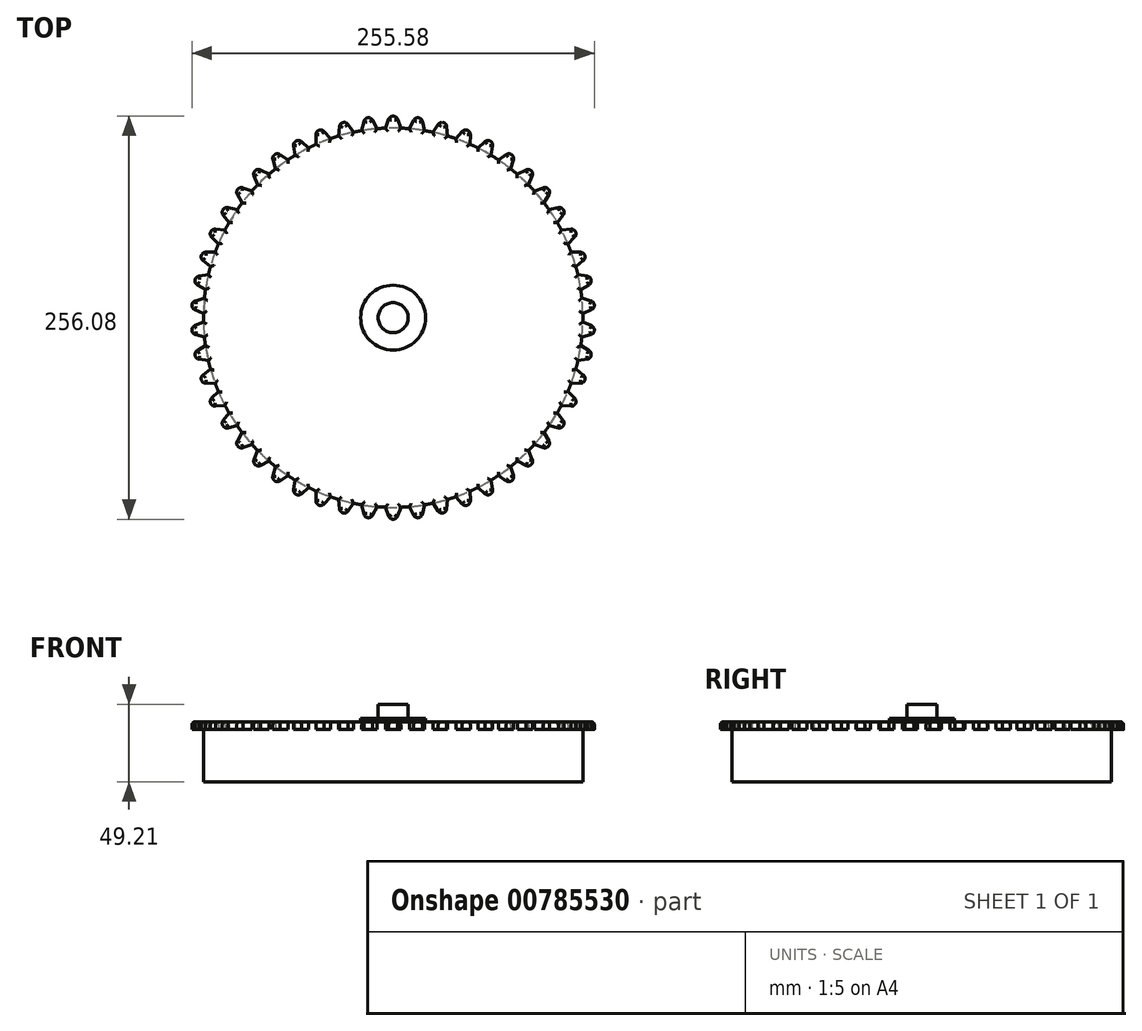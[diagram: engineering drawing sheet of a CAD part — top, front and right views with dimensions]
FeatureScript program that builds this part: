
annotation { "Feature Type Name" : "Feature", "Feature Type Description" : "" }
export const myFeature = defineFeature(function(context is Context, id is Id, definition is map)
    precondition{}
    {
        {
            var Q0;
            Q0=qCreatedBy(makeId("Top.planeOp"),FACE);
            var sketch = newSketch(context, id + "F0", { "sketchPlane" : qUnion([Q0])});
            skCircle(sketch, "E0", {"center": v(0, 0) * mm, "radius": 120.5 * mm});
            skSolve(sketch);
        }
        {
            var Q0;
            Q0 = qSketchRegion(id + "F0", true);
            extrude(context, id + "F1", {"entities" : qUnion([Q0]), "depth" : 38.1 * mm, "offsetDistance" : 25 * mm});
        }
        {
            var Q0;
            Q0=makeQuery(id+"F1.opExtrude","CAP_FACE",FACE,{"disambiguationData":[OSD([sQuery(id+"F0.wireOp",EDGE,"E0")])],"isStart":false});
            var sketch = newSketch(context, id + "F2", { "sketchPlane" : qUnion([Q0])});
            skCircle(sketch, "E1", {"center": v(0, 0) * mm, "radius": 9.53 * mm});
            skSolve(sketch);
        }
        {
            var Q0;
            Q0 = qSketchRegion(id + "F2", true);
            extrude(context, id + "F3", {"entities" : qUnion([Q0]), "operationType" : NewBodyOperationType.ADD, "depth" : 11.1 * mm, "offsetDistance" : 25 * mm});
        }
        {
            var Q0;
            Q0=makeQuery(id+"F1.opExtrude","CAP_FACE",FACE,{"disambiguationData":[OSD([sQuery(id+"F0.wireOp",EDGE,"E0")])],"isStart":false});
            var sketch = newSketch(context, id + "F4", { "sketchPlane" : qUnion([Q0])});
            skCircle(sketch, "E2", {"center": v(0, 0) * mm, "radius": 20.64 * mm});
            skSolve(sketch);
        }
        {
            var Q0;
            Q0 = qSketchRegion(id + "F4", true);
            extrude(context, id + "F5", {"entities" : qUnion([Q0]), "operationType" : NewBodyOperationType.ADD, "depth" : 2 * mm, "offsetDistance" : 25 * mm});
        }
        {
            var Q0;
            Q0=makeQuery(id+"F1.opExtrude","CAP_FACE",FACE,{"disambiguationData":[OSD([sQuery(id+"F0.wireOp",EDGE,"E0")])],"isStart":false});
            var sketch = newSketch(context, id + "F6", { "sketchPlane" : qUnion([Q0])});
            skLineSegment(sketch, "E3", {"start": v(-5, 120) * mm, "end": v(-2.8, 126.04) * mm});
            skLineSegment(sketch, "E4", {"start": v(-2.8, 126.04) * mm, "end": v(2.8, 126.04) * mm, "construction": true});
            skLineSegment(sketch, "E5", {"start": v(2.8, 126.04) * mm, "end": v(5, 120) * mm});
            skArc(sketch, "E6", {"start": v(2.8, 126.04) * mm, "mid": v(0, 128.04) * mm, "end": v(-2.8, 126.04) * mm});
            skPoint(sketch, "E7", {"position": v(0, 128.04) * mm});
            skLineSegment(sketch, "E8", {"start": v(5, 120) * mm, "end": v(7.52, 119.56) * mm});
            skLineSegment(sketch, "E9", {"start": v(-5, 120) * mm, "end": v(-7.52, 119.56) * mm});
            skArc(sketch, "E10.1.0", {"start": v(-13.02, 125.4) * mm, "mid": v(-16.05, 127.03) * mm, "end": v(-18.58, 124.7) * mm});
            skLineSegment(sketch, "E10.1.1", {"start": v(-10.08, 119.68) * mm, "end": v(-7.52, 119.56) * mm});
            skPoint(sketch, "E10.1.2", {"position": v(-16.05, 127.03) * mm});
            skLineSegment(sketch, "E10.1.3", {"start": v(-13.02, 125.4) * mm, "end": v(-10.08, 119.68) * mm});
            skLineSegment(sketch, "E10.1.4", {"start": v(-20, 118.43) * mm, "end": v(-22.45, 117.67) * mm});
            skLineSegment(sketch, "E10.1.5", {"start": v(-20, 118.43) * mm, "end": v(-18.58, 124.7) * mm});
            skLineSegment(sketch, "E10.1.6", {"start": v(-18.58, 124.7) * mm, "end": v(-13.02, 125.4) * mm, "construction": true});
            skArc(sketch, "E10.2.0", {"start": v(-28.63, 122.78) * mm, "mid": v(-31.84, 124.02) * mm, "end": v(-34.06, 121.38) * mm});
            skLineSegment(sketch, "E10.2.1", {"start": v(-25, 117.47) * mm, "end": v(-22.45, 117.67) * mm});
            skPoint(sketch, "E10.2.2", {"position": v(-31.84, 124.02) * mm});
            skLineSegment(sketch, "E10.2.3", {"start": v(-28.63, 122.78) * mm, "end": v(-25, 117.47) * mm});
            skLineSegment(sketch, "E10.2.4", {"start": v(-34.69, 114.99) * mm, "end": v(-37.02, 113.93) * mm});
            skLineSegment(sketch, "E10.2.5", {"start": v(-34.69, 114.99) * mm, "end": v(-34.06, 121.38) * mm});
            skLineSegment(sketch, "E10.2.6", {"start": v(-34.06, 121.38) * mm, "end": v(-28.63, 122.78) * mm, "construction": true});
            skArc(sketch, "E10.3.0", {"start": v(-43.8, 118.22) * mm, "mid": v(-47.13, 119.05) * mm, "end": v(-49, 116.16) * mm});
            skLineSegment(sketch, "E10.3.1", {"start": v(-39.53, 113.41) * mm, "end": v(-37.02, 113.93) * mm});
            skPoint(sketch, "E10.3.2", {"position": v(-47.13, 119.05) * mm});
            skLineSegment(sketch, "E10.3.3", {"start": v(-43.8, 118.22) * mm, "end": v(-39.53, 113.41) * mm});
            skLineSegment(sketch, "E10.3.4", {"start": v(-48.82, 109.73) * mm, "end": v(-51, 108.4) * mm});
            skLineSegment(sketch, "E10.3.5", {"start": v(-48.82, 109.73) * mm, "end": v(-49, 116.16) * mm});
            skLineSegment(sketch, "E10.3.6", {"start": v(-49, 116.16) * mm, "end": v(-43.8, 118.22) * mm, "construction": true});
            skArc(sketch, "E10.4.0", {"start": v(-58.26, 111.8) * mm, "mid": v(-61.68, 112.2) * mm, "end": v(-63.18, 109.1) * mm});
            skLineSegment(sketch, "E10.4.1", {"start": v(-53.43, 107.57) * mm, "end": v(-51, 108.4) * mm});
            skPoint(sketch, "E10.4.2", {"position": v(-61.68, 112.2) * mm});
            skLineSegment(sketch, "E10.4.3", {"start": v(-58.26, 111.8) * mm, "end": v(-53.43, 107.57) * mm});
            skLineSegment(sketch, "E10.4.4", {"start": v(-62.2, 102.75) * mm, "end": v(-64.19, 101.14) * mm});
            skLineSegment(sketch, "E10.4.5", {"start": v(-62.2, 102.75) * mm, "end": v(-63.18, 109.1) * mm});
            skLineSegment(sketch, "E10.4.6", {"start": v(-63.18, 109.1) * mm, "end": v(-58.26, 111.8) * mm, "construction": true});
            skArc(sketch, "E10.5.0", {"start": v(-71.82, 103.61) * mm, "mid": v(-75.26, 103.58) * mm, "end": v(-76.35, 100.32) * mm});
            skLineSegment(sketch, "E10.5.1", {"start": v(-66.49, 100.02) * mm, "end": v(-64.19, 101.14) * mm});
            skPoint(sketch, "E10.5.2", {"position": v(-75.26, 103.58) * mm});
            skLineSegment(sketch, "E10.5.3", {"start": v(-71.82, 103.61) * mm, "end": v(-66.49, 100.02) * mm});
            skLineSegment(sketch, "E10.5.4", {"start": v(-74.58, 94.14) * mm, "end": v(-76.36, 92.3) * mm});
            skLineSegment(sketch, "E10.5.5", {"start": v(-74.58, 94.14) * mm, "end": v(-76.35, 100.32) * mm});
            skLineSegment(sketch, "E10.5.6", {"start": v(-76.35, 100.32) * mm, "end": v(-71.82, 103.61) * mm, "construction": true});
            skArc(sketch, "E10.6.0", {"start": v(-84.24, 93.8) * mm, "mid": v(-87.65, 93.34) * mm, "end": v(-88.32, 89.96) * mm});
            skLineSegment(sketch, "E10.6.1", {"start": v(-78.5, 90.9) * mm, "end": v(-76.36, 92.3) * mm});
            skPoint(sketch, "E10.6.2", {"position": v(-87.65, 93.34) * mm});
            skLineSegment(sketch, "E10.6.3", {"start": v(-84.24, 93.8) * mm, "end": v(-78.5, 90.9) * mm});
            skLineSegment(sketch, "E10.6.4", {"start": v(-85.8, 84.05) * mm, "end": v(-87.32, 82) * mm});
            skLineSegment(sketch, "E10.6.5", {"start": v(-85.8, 84.05) * mm, "end": v(-88.32, 89.96) * mm});
            skLineSegment(sketch, "E10.6.6", {"start": v(-88.32, 89.96) * mm, "end": v(-84.24, 93.8) * mm, "construction": true});
            skArc(sketch, "E10.7.0", {"start": v(-95.33, 82.5) * mm, "mid": v(-98.66, 81.61) * mm, "end": v(-98.9, 78.18) * mm});
            skLineSegment(sketch, "E10.7.1", {"start": v(-89.27, 80.34) * mm, "end": v(-87.32, 82) * mm});
            skPoint(sketch, "E10.7.2", {"position": v(-98.66, 81.61) * mm});
            skLineSegment(sketch, "E10.7.3", {"start": v(-95.33, 82.5) * mm, "end": v(-89.27, 80.34) * mm});
            skLineSegment(sketch, "E10.7.4", {"start": v(-95.65, 72.64) * mm, "end": v(-96.91, 70.41) * mm});
            skLineSegment(sketch, "E10.7.5", {"start": v(-95.65, 72.64) * mm, "end": v(-98.9, 78.18) * mm});
            skLineSegment(sketch, "E10.7.6", {"start": v(-98.9, 78.18) * mm, "end": v(-95.33, 82.5) * mm, "construction": true});
            skArc(sketch, "E10.8.0", {"start": v(-104.92, 69.9) * mm, "mid": v(-108.1, 68.6) * mm, "end": v(-107.92, 65.17) * mm});
            skLineSegment(sketch, "E10.8.1", {"start": v(-98.64, 68.52) * mm, "end": v(-96.91, 70.41) * mm});
            skPoint(sketch, "E10.8.2", {"position": v(-108.1, 68.6) * mm});
            skLineSegment(sketch, "E10.8.3", {"start": v(-104.92, 69.9) * mm, "end": v(-98.64, 68.52) * mm});
            skLineSegment(sketch, "E10.8.4", {"start": v(-104, 60.08) * mm, "end": v(-104.97, 57.7) * mm});
            skLineSegment(sketch, "E10.8.5", {"start": v(-104, 60.08) * mm, "end": v(-107.92, 65.17) * mm});
            skLineSegment(sketch, "E10.8.6", {"start": v(-107.92, 65.17) * mm, "end": v(-104.92, 69.9) * mm, "construction": true});
            skArc(sketch, "E10.9.0", {"start": v(-112.85, 56.2) * mm, "mid": v(-115.85, 54.52) * mm, "end": v(-115.24, 51.13) * mm});
            skLineSegment(sketch, "E10.9.1", {"start": v(-106.45, 55.62) * mm, "end": v(-104.97, 57.7) * mm});
            skPoint(sketch, "E10.9.2", {"position": v(-115.85, 54.52) * mm});
            skLineSegment(sketch, "E10.9.3", {"start": v(-112.85, 56.2) * mm, "end": v(-106.45, 55.62) * mm});
            skLineSegment(sketch, "E10.9.4", {"start": v(-110.7, 46.57) * mm, "end": v(-111.38, 44.1) * mm});
            skLineSegment(sketch, "E10.9.5", {"start": v(-110.7, 46.57) * mm, "end": v(-115.24, 51.13) * mm});
            skLineSegment(sketch, "E10.9.6", {"start": v(-115.24, 51.13) * mm, "end": v(-112.85, 56.2) * mm, "construction": true});
            skArc(sketch, "E10.10.0", {"start": v(-119, 41.61) * mm, "mid": v(-121.77, 39.57) * mm, "end": v(-120.74, 36.28) * mm});
            skLineSegment(sketch, "E10.10.1", {"start": v(-112.58, 41.84) * mm, "end": v(-111.38, 44.1) * mm});
            skPoint(sketch, "E10.10.2", {"position": v(-121.77, 39.57) * mm});
            skLineSegment(sketch, "E10.10.3", {"start": v(-119, 41.61) * mm, "end": v(-112.58, 41.84) * mm});
            skLineSegment(sketch, "E10.10.4", {"start": v(-115.67, 32.33) * mm, "end": v(-116.03, 29.8) * mm});
            skLineSegment(sketch, "E10.10.5", {"start": v(-115.67, 32.33) * mm, "end": v(-120.74, 36.28) * mm});
            skLineSegment(sketch, "E10.10.6", {"start": v(-120.74, 36.28) * mm, "end": v(-119, 41.61) * mm, "construction": true});
            skArc(sketch, "E10.11.0", {"start": v(-123.28, 26.37) * mm, "mid": v(-125.77, 24) * mm, "end": v(-124.33, 20.86) * mm});
            skLineSegment(sketch, "E10.11.1", {"start": v(-116.94, 27.4) * mm, "end": v(-116.03, 29.8) * mm});
            skPoint(sketch, "E10.11.2", {"position": v(-125.77, 24) * mm});
            skLineSegment(sketch, "E10.11.3", {"start": v(-123.28, 26.37) * mm, "end": v(-116.94, 27.4) * mm});
            skLineSegment(sketch, "E10.11.4", {"start": v(-118.81, 17.57) * mm, "end": v(-118.85, 15.01) * mm});
            skLineSegment(sketch, "E10.11.5", {"start": v(-118.81, 17.57) * mm, "end": v(-124.33, 20.86) * mm});
            skLineSegment(sketch, "E10.11.6", {"start": v(-124.33, 20.86) * mm, "end": v(-123.28, 26.37) * mm, "construction": true});
            skArc(sketch, "E10.12.0", {"start": v(-125.61, 10.71) * mm, "mid": v(-127.79, 8.04) * mm, "end": v(-125.97, 5.12) * mm});
            skLineSegment(sketch, "E10.12.1", {"start": v(-119.45, 12.52) * mm, "end": v(-118.85, 15.01) * mm});
            skPoint(sketch, "E10.12.2", {"position": v(-127.79, 8.04) * mm});
            skLineSegment(sketch, "E10.12.3", {"start": v(-125.61, 10.71) * mm, "end": v(-119.45, 12.52) * mm});
            skLineSegment(sketch, "E10.12.4", {"start": v(-120.08, 2.54) * mm, "end": v(-119.8, 0) * mm});
            skLineSegment(sketch, "E10.12.5", {"start": v(-120.08, 2.54) * mm, "end": v(-125.97, 5.12) * mm});
            skLineSegment(sketch, "E10.12.6", {"start": v(-125.97, 5.12) * mm, "end": v(-125.61, 10.71) * mm, "construction": true});
            skArc(sketch, "E10.13.0", {"start": v(-125.97, -5.12) * mm, "mid": v(-127.79, -8.04) * mm, "end": v(-125.61, -10.71) * mm});
            skLineSegment(sketch, "E10.13.1", {"start": v(-120.08, -2.55) * mm, "end": v(-119.8, 0) * mm});
            skPoint(sketch, "E10.13.2", {"position": v(-127.79, -8.04) * mm});
            skLineSegment(sketch, "E10.13.3", {"start": v(-125.97, -5.12) * mm, "end": v(-120.08, -2.55) * mm});
            skLineSegment(sketch, "E10.13.4", {"start": v(-119.45, -12.53) * mm, "end": v(-118.85, -15.01) * mm});
            skLineSegment(sketch, "E10.13.5", {"start": v(-119.45, -12.53) * mm, "end": v(-125.61, -10.71) * mm});
            skLineSegment(sketch, "E10.13.6", {"start": v(-125.61, -10.71) * mm, "end": v(-125.97, -5.12) * mm, "construction": true});
            skArc(sketch, "E10.14.0", {"start": v(-124.33, -20.87) * mm, "mid": v(-125.77, -24) * mm, "end": v(-123.28, -26.37) * mm});
            skLineSegment(sketch, "E10.14.1", {"start": v(-118.81, -17.58) * mm, "end": v(-118.85, -15.01) * mm});
            skPoint(sketch, "E10.14.2", {"position": v(-125.77, -24) * mm});
            skLineSegment(sketch, "E10.14.3", {"start": v(-124.33, -20.87) * mm, "end": v(-118.81, -17.58) * mm});
            skLineSegment(sketch, "E10.14.4", {"start": v(-116.94, -27.4) * mm, "end": v(-116.03, -29.8) * mm});
            skLineSegment(sketch, "E10.14.5", {"start": v(-116.94, -27.4) * mm, "end": v(-123.28, -26.37) * mm});
            skLineSegment(sketch, "E10.14.6", {"start": v(-123.28, -26.37) * mm, "end": v(-124.33, -20.87) * mm, "construction": true});
            skArc(sketch, "E10.15.0", {"start": v(-120.74, -36.28) * mm, "mid": v(-121.77, -39.57) * mm, "end": v(-119, -41.61) * mm});
            skLineSegment(sketch, "E10.15.1", {"start": v(-115.67, -32.33) * mm, "end": v(-116.03, -29.8) * mm});
            skPoint(sketch, "E10.15.2", {"position": v(-121.77, -39.57) * mm});
            skLineSegment(sketch, "E10.15.3", {"start": v(-120.74, -36.28) * mm, "end": v(-115.67, -32.33) * mm});
            skLineSegment(sketch, "E10.15.4", {"start": v(-112.58, -41.84) * mm, "end": v(-111.38, -44.1) * mm});
            skLineSegment(sketch, "E10.15.5", {"start": v(-112.58, -41.84) * mm, "end": v(-119, -41.61) * mm});
            skLineSegment(sketch, "E10.15.6", {"start": v(-119, -41.61) * mm, "end": v(-120.74, -36.28) * mm, "construction": true});
            skArc(sketch, "E10.16.0", {"start": v(-115.24, -51.13) * mm, "mid": v(-115.85, -54.52) * mm, "end": v(-112.85, -56.2) * mm});
            skLineSegment(sketch, "E10.16.1", {"start": v(-110.7, -46.57) * mm, "end": v(-111.38, -44.1) * mm});
            skPoint(sketch, "E10.16.2", {"position": v(-115.85, -54.52) * mm});
            skLineSegment(sketch, "E10.16.3", {"start": v(-115.24, -51.13) * mm, "end": v(-110.7, -46.57) * mm});
            skLineSegment(sketch, "E10.16.4", {"start": v(-106.45, -55.62) * mm, "end": v(-104.97, -57.71) * mm});
            skLineSegment(sketch, "E10.16.5", {"start": v(-106.45, -55.62) * mm, "end": v(-112.85, -56.2) * mm});
            skLineSegment(sketch, "E10.16.6", {"start": v(-112.85, -56.2) * mm, "end": v(-115.24, -51.13) * mm, "construction": true});
            skArc(sketch, "E10.17.0", {"start": v(-107.92, -65.17) * mm, "mid": v(-108.1, -68.6) * mm, "end": v(-104.92, -69.9) * mm});
            skLineSegment(sketch, "E10.17.1", {"start": v(-104, -60.08) * mm, "end": v(-104.97, -57.71) * mm});
            skPoint(sketch, "E10.17.2", {"position": v(-108.1, -68.6) * mm});
            skLineSegment(sketch, "E10.17.3", {"start": v(-107.92, -65.17) * mm, "end": v(-104, -60.08) * mm});
            skLineSegment(sketch, "E10.17.4", {"start": v(-98.64, -68.52) * mm, "end": v(-96.91, -70.41) * mm});
            skLineSegment(sketch, "E10.17.5", {"start": v(-98.64, -68.52) * mm, "end": v(-104.92, -69.9) * mm});
            skLineSegment(sketch, "E10.17.6", {"start": v(-104.92, -69.9) * mm, "end": v(-107.92, -65.17) * mm, "construction": true});
            skArc(sketch, "E10.18.0", {"start": v(-98.9, -78.18) * mm, "mid": v(-98.66, -81.62) * mm, "end": v(-95.33, -82.5) * mm});
            skLineSegment(sketch, "E10.18.1", {"start": v(-95.65, -72.64) * mm, "end": v(-96.91, -70.41) * mm});
            skPoint(sketch, "E10.18.2", {"position": v(-98.66, -81.62) * mm});
            skLineSegment(sketch, "E10.18.3", {"start": v(-98.9, -78.18) * mm, "end": v(-95.65, -72.64) * mm});
            skLineSegment(sketch, "E10.18.4", {"start": v(-89.27, -80.34) * mm, "end": v(-87.32, -82) * mm});
            skLineSegment(sketch, "E10.18.5", {"start": v(-89.27, -80.34) * mm, "end": v(-95.33, -82.5) * mm});
            skLineSegment(sketch, "E10.18.6", {"start": v(-95.33, -82.5) * mm, "end": v(-98.9, -78.18) * mm, "construction": true});
            skArc(sketch, "E10.19.0", {"start": v(-88.32, -89.96) * mm, "mid": v(-87.65, -93.34) * mm, "end": v(-84.24, -93.8) * mm});
            skLineSegment(sketch, "E10.19.1", {"start": v(-85.8, -84.05) * mm, "end": v(-87.32, -82) * mm});
            skPoint(sketch, "E10.19.2", {"position": v(-87.65, -93.34) * mm});
            skLineSegment(sketch, "E10.19.3", {"start": v(-88.32, -89.96) * mm, "end": v(-85.8, -84.05) * mm});
            skLineSegment(sketch, "E10.19.4", {"start": v(-78.5, -90.9) * mm, "end": v(-76.36, -92.3) * mm});
            skLineSegment(sketch, "E10.19.5", {"start": v(-78.5, -90.9) * mm, "end": v(-84.24, -93.8) * mm});
            skLineSegment(sketch, "E10.19.6", {"start": v(-84.24, -93.8) * mm, "end": v(-88.32, -89.96) * mm, "construction": true});
            skArc(sketch, "E10.20.0", {"start": v(-76.35, -100.32) * mm, "mid": v(-75.26, -103.59) * mm, "end": v(-71.82, -103.62) * mm});
            skLineSegment(sketch, "E10.20.1", {"start": v(-74.58, -94.14) * mm, "end": v(-76.36, -92.3) * mm});
            skPoint(sketch, "E10.20.2", {"position": v(-75.26, -103.59) * mm});
            skLineSegment(sketch, "E10.20.3", {"start": v(-76.35, -100.32) * mm, "end": v(-74.58, -94.14) * mm});
            skLineSegment(sketch, "E10.20.4", {"start": v(-66.49, -100.02) * mm, "end": v(-64.19, -101.14) * mm});
            skLineSegment(sketch, "E10.20.5", {"start": v(-66.49, -100.02) * mm, "end": v(-71.82, -103.62) * mm});
            skLineSegment(sketch, "E10.20.6", {"start": v(-71.82, -103.62) * mm, "end": v(-76.35, -100.32) * mm, "construction": true});
            skArc(sketch, "E10.21.0", {"start": v(-63.18, -109.1) * mm, "mid": v(-61.68, -112.2) * mm, "end": v(-58.26, -111.8) * mm});
            skLineSegment(sketch, "E10.21.1", {"start": v(-62.2, -102.75) * mm, "end": v(-64.19, -101.14) * mm});
            skPoint(sketch, "E10.21.2", {"position": v(-61.68, -112.2) * mm});
            skLineSegment(sketch, "E10.21.3", {"start": v(-63.18, -109.1) * mm, "end": v(-62.2, -102.75) * mm});
            skLineSegment(sketch, "E10.21.4", {"start": v(-53.43, -107.57) * mm, "end": v(-51, -108.4) * mm});
            skLineSegment(sketch, "E10.21.5", {"start": v(-53.43, -107.57) * mm, "end": v(-58.26, -111.8) * mm});
            skLineSegment(sketch, "E10.21.6", {"start": v(-58.26, -111.8) * mm, "end": v(-63.18, -109.1) * mm, "construction": true});
            skArc(sketch, "E10.22.0", {"start": v(-49, -116.16) * mm, "mid": v(-47.13, -119.05) * mm, "end": v(-43.8, -118.22) * mm});
            skLineSegment(sketch, "E10.22.1", {"start": v(-48.82, -109.73) * mm, "end": v(-51, -108.4) * mm});
            skPoint(sketch, "E10.22.2", {"position": v(-47.13, -119.05) * mm});
            skLineSegment(sketch, "E10.22.3", {"start": v(-49, -116.16) * mm, "end": v(-48.82, -109.73) * mm});
            skLineSegment(sketch, "E10.22.4", {"start": v(-39.53, -113.42) * mm, "end": v(-37.02, -113.93) * mm});
            skLineSegment(sketch, "E10.22.5", {"start": v(-39.53, -113.42) * mm, "end": v(-43.8, -118.22) * mm});
            skLineSegment(sketch, "E10.22.6", {"start": v(-43.8, -118.22) * mm, "end": v(-49, -116.16) * mm, "construction": true});
            skArc(sketch, "E10.23.0", {"start": v(-34.06, -121.38) * mm, "mid": v(-31.84, -124.02) * mm, "end": v(-28.63, -122.78) * mm});
            skLineSegment(sketch, "E10.23.1", {"start": v(-34.69, -114.99) * mm, "end": v(-37.02, -113.93) * mm});
            skPoint(sketch, "E10.23.2", {"position": v(-31.84, -124.02) * mm});
            skLineSegment(sketch, "E10.23.3", {"start": v(-34.06, -121.38) * mm, "end": v(-34.69, -114.99) * mm});
            skLineSegment(sketch, "E10.23.4", {"start": v(-25, -117.47) * mm, "end": v(-22.45, -117.67) * mm});
            skLineSegment(sketch, "E10.23.5", {"start": v(-25, -117.47) * mm, "end": v(-28.63, -122.78) * mm});
            skLineSegment(sketch, "E10.23.6", {"start": v(-28.63, -122.78) * mm, "end": v(-34.06, -121.38) * mm, "construction": true});
            skArc(sketch, "E10.24.0", {"start": v(-18.58, -124.7) * mm, "mid": v(-16.05, -127.03) * mm, "end": v(-13.02, -125.4) * mm});
            skLineSegment(sketch, "E10.24.1", {"start": v(-20, -118.43) * mm, "end": v(-22.45, -117.67) * mm});
            skPoint(sketch, "E10.24.2", {"position": v(-16.05, -127.03) * mm});
            skLineSegment(sketch, "E10.24.3", {"start": v(-18.58, -124.7) * mm, "end": v(-20, -118.43) * mm});
            skLineSegment(sketch, "E10.24.4", {"start": v(-10.08, -119.68) * mm, "end": v(-7.52, -119.56) * mm});
            skLineSegment(sketch, "E10.24.5", {"start": v(-10.08, -119.68) * mm, "end": v(-13.02, -125.4) * mm});
            skLineSegment(sketch, "E10.24.6", {"start": v(-13.02, -125.4) * mm, "end": v(-18.58, -124.7) * mm, "construction": true});
            skArc(sketch, "E10.25.0", {"start": v(-2.8, -126.04) * mm, "mid": v(0, -128.04) * mm, "end": v(2.8, -126.04) * mm});
            skLineSegment(sketch, "E10.25.1", {"start": v(-5, -120) * mm, "end": v(-7.52, -119.56) * mm});
            skPoint(sketch, "E10.25.2", {"position": v(0, -128.04) * mm});
            skLineSegment(sketch, "E10.25.3", {"start": v(-2.8, -126.04) * mm, "end": v(-5, -120) * mm});
            skLineSegment(sketch, "E10.25.4", {"start": v(5, -120) * mm, "end": v(7.52, -119.56) * mm});
            skLineSegment(sketch, "E10.25.5", {"start": v(5, -120) * mm, "end": v(2.8, -126.04) * mm});
            skLineSegment(sketch, "E10.25.6", {"start": v(2.8, -126.04) * mm, "end": v(-2.8, -126.04) * mm, "construction": true});
            skArc(sketch, "E10.26.0", {"start": v(13.02, -125.4) * mm, "mid": v(16.05, -127.03) * mm, "end": v(18.58, -124.7) * mm});
            skLineSegment(sketch, "E10.26.1", {"start": v(10.08, -119.68) * mm, "end": v(7.52, -119.56) * mm});
            skPoint(sketch, "E10.26.2", {"position": v(16.05, -127.03) * mm});
            skLineSegment(sketch, "E10.26.3", {"start": v(13.02, -125.4) * mm, "end": v(10.08, -119.68) * mm});
            skLineSegment(sketch, "E10.26.4", {"start": v(20, -118.43) * mm, "end": v(22.45, -117.67) * mm});
            skLineSegment(sketch, "E10.26.5", {"start": v(20, -118.43) * mm, "end": v(18.58, -124.7) * mm});
            skLineSegment(sketch, "E10.26.6", {"start": v(18.58, -124.7) * mm, "end": v(13.02, -125.4) * mm, "construction": true});
            skArc(sketch, "E10.27.0", {"start": v(28.63, -122.78) * mm, "mid": v(31.84, -124.02) * mm, "end": v(34.06, -121.38) * mm});
            skLineSegment(sketch, "E10.27.1", {"start": v(25, -117.47) * mm, "end": v(22.45, -117.67) * mm});
            skPoint(sketch, "E10.27.2", {"position": v(31.84, -124.02) * mm});
            skLineSegment(sketch, "E10.27.3", {"start": v(28.63, -122.78) * mm, "end": v(25, -117.47) * mm});
            skLineSegment(sketch, "E10.27.4", {"start": v(34.69, -114.99) * mm, "end": v(37.02, -113.93) * mm});
            skLineSegment(sketch, "E10.27.5", {"start": v(34.69, -114.99) * mm, "end": v(34.06, -121.38) * mm});
            skLineSegment(sketch, "E10.27.6", {"start": v(34.06, -121.38) * mm, "end": v(28.63, -122.78) * mm, "construction": true});
            skArc(sketch, "E10.28.0", {"start": v(43.8, -118.22) * mm, "mid": v(47.13, -119.05) * mm, "end": v(49, -116.16) * mm});
            skLineSegment(sketch, "E10.28.1", {"start": v(39.53, -113.42) * mm, "end": v(37.02, -113.93) * mm});
            skPoint(sketch, "E10.28.2", {"position": v(47.13, -119.05) * mm});
            skLineSegment(sketch, "E10.28.3", {"start": v(43.8, -118.22) * mm, "end": v(39.53, -113.42) * mm});
            skLineSegment(sketch, "E10.28.4", {"start": v(48.82, -109.73) * mm, "end": v(51, -108.4) * mm});
            skLineSegment(sketch, "E10.28.5", {"start": v(48.82, -109.73) * mm, "end": v(49, -116.16) * mm});
            skLineSegment(sketch, "E10.28.6", {"start": v(49, -116.16) * mm, "end": v(43.8, -118.22) * mm, "construction": true});
            skArc(sketch, "E10.29.0", {"start": v(58.26, -111.8) * mm, "mid": v(61.68, -112.2) * mm, "end": v(63.18, -109.1) * mm});
            skLineSegment(sketch, "E10.29.1", {"start": v(53.43, -107.57) * mm, "end": v(51, -108.4) * mm});
            skPoint(sketch, "E10.29.2", {"position": v(61.68, -112.2) * mm});
            skLineSegment(sketch, "E10.29.3", {"start": v(58.26, -111.8) * mm, "end": v(53.43, -107.57) * mm});
            skLineSegment(sketch, "E10.29.4", {"start": v(62.2, -102.75) * mm, "end": v(64.19, -101.14) * mm});
            skLineSegment(sketch, "E10.29.5", {"start": v(62.2, -102.75) * mm, "end": v(63.18, -109.1) * mm});
            skLineSegment(sketch, "E10.29.6", {"start": v(63.18, -109.1) * mm, "end": v(58.26, -111.8) * mm, "construction": true});
            skArc(sketch, "E10.30.0", {"start": v(71.82, -103.62) * mm, "mid": v(75.26, -103.59) * mm, "end": v(76.35, -100.32) * mm});
            skLineSegment(sketch, "E10.30.1", {"start": v(66.49, -100.02) * mm, "end": v(64.19, -101.14) * mm});
            skPoint(sketch, "E10.30.2", {"position": v(75.26, -103.59) * mm});
            skLineSegment(sketch, "E10.30.3", {"start": v(71.82, -103.62) * mm, "end": v(66.49, -100.02) * mm});
            skLineSegment(sketch, "E10.30.4", {"start": v(74.58, -94.14) * mm, "end": v(76.36, -92.3) * mm});
            skLineSegment(sketch, "E10.30.5", {"start": v(74.58, -94.14) * mm, "end": v(76.35, -100.32) * mm});
            skLineSegment(sketch, "E10.30.6", {"start": v(76.35, -100.32) * mm, "end": v(71.82, -103.62) * mm, "construction": true});
            skArc(sketch, "E10.31.0", {"start": v(84.24, -93.8) * mm, "mid": v(87.65, -93.34) * mm, "end": v(88.32, -89.96) * mm});
            skLineSegment(sketch, "E10.31.1", {"start": v(78.5, -90.9) * mm, "end": v(76.36, -92.3) * mm});
            skPoint(sketch, "E10.31.2", {"position": v(87.65, -93.34) * mm});
            skLineSegment(sketch, "E10.31.3", {"start": v(84.24, -93.8) * mm, "end": v(78.5, -90.9) * mm});
            skLineSegment(sketch, "E10.31.4", {"start": v(85.8, -84.05) * mm, "end": v(87.32, -82) * mm});
            skLineSegment(sketch, "E10.31.5", {"start": v(85.8, -84.05) * mm, "end": v(88.32, -89.96) * mm});
            skLineSegment(sketch, "E10.31.6", {"start": v(88.32, -89.96) * mm, "end": v(84.24, -93.8) * mm, "construction": true});
            skArc(sketch, "E10.32.0", {"start": v(95.33, -82.5) * mm, "mid": v(98.66, -81.62) * mm, "end": v(98.9, -78.18) * mm});
            skLineSegment(sketch, "E10.32.1", {"start": v(89.27, -80.34) * mm, "end": v(87.32, -82) * mm});
            skPoint(sketch, "E10.32.2", {"position": v(98.66, -81.62) * mm});
            skLineSegment(sketch, "E10.32.3", {"start": v(95.33, -82.5) * mm, "end": v(89.27, -80.34) * mm});
            skLineSegment(sketch, "E10.32.4", {"start": v(95.65, -72.64) * mm, "end": v(96.91, -70.41) * mm});
            skLineSegment(sketch, "E10.32.5", {"start": v(95.65, -72.64) * mm, "end": v(98.9, -78.18) * mm});
            skLineSegment(sketch, "E10.32.6", {"start": v(98.9, -78.18) * mm, "end": v(95.33, -82.5) * mm, "construction": true});
            skArc(sketch, "E10.33.0", {"start": v(104.92, -69.9) * mm, "mid": v(108.1, -68.6) * mm, "end": v(107.92, -65.17) * mm});
            skLineSegment(sketch, "E10.33.1", {"start": v(98.64, -68.52) * mm, "end": v(96.91, -70.41) * mm});
            skPoint(sketch, "E10.33.2", {"position": v(108.1, -68.6) * mm});
            skLineSegment(sketch, "E10.33.3", {"start": v(104.92, -69.9) * mm, "end": v(98.64, -68.52) * mm});
            skLineSegment(sketch, "E10.33.4", {"start": v(104, -60.08) * mm, "end": v(104.97, -57.71) * mm});
            skLineSegment(sketch, "E10.33.5", {"start": v(104, -60.08) * mm, "end": v(107.92, -65.17) * mm});
            skLineSegment(sketch, "E10.33.6", {"start": v(107.92, -65.17) * mm, "end": v(104.92, -69.9) * mm, "construction": true});
            skArc(sketch, "E10.34.0", {"start": v(112.85, -56.2) * mm, "mid": v(115.85, -54.52) * mm, "end": v(115.24, -51.13) * mm});
            skLineSegment(sketch, "E10.34.1", {"start": v(106.45, -55.62) * mm, "end": v(104.97, -57.71) * mm});
            skPoint(sketch, "E10.34.2", {"position": v(115.85, -54.52) * mm});
            skLineSegment(sketch, "E10.34.3", {"start": v(112.85, -56.2) * mm, "end": v(106.45, -55.62) * mm});
            skLineSegment(sketch, "E10.34.4", {"start": v(110.7, -46.57) * mm, "end": v(111.38, -44.1) * mm});
            skLineSegment(sketch, "E10.34.5", {"start": v(110.7, -46.57) * mm, "end": v(115.24, -51.13) * mm});
            skLineSegment(sketch, "E10.34.6", {"start": v(115.24, -51.13) * mm, "end": v(112.85, -56.2) * mm, "construction": true});
            skArc(sketch, "E10.35.0", {"start": v(119, -41.61) * mm, "mid": v(121.77, -39.57) * mm, "end": v(120.74, -36.28) * mm});
            skLineSegment(sketch, "E10.35.1", {"start": v(112.58, -41.84) * mm, "end": v(111.38, -44.1) * mm});
            skPoint(sketch, "E10.35.2", {"position": v(121.77, -39.57) * mm});
            skLineSegment(sketch, "E10.35.3", {"start": v(119, -41.61) * mm, "end": v(112.58, -41.84) * mm});
            skLineSegment(sketch, "E10.35.4", {"start": v(115.67, -32.33) * mm, "end": v(116.03, -29.8) * mm});
            skLineSegment(sketch, "E10.35.5", {"start": v(115.67, -32.33) * mm, "end": v(120.74, -36.28) * mm});
            skLineSegment(sketch, "E10.35.6", {"start": v(120.74, -36.28) * mm, "end": v(119, -41.61) * mm, "construction": true});
            skArc(sketch, "E10.36.0", {"start": v(123.28, -26.37) * mm, "mid": v(125.77, -24) * mm, "end": v(124.33, -20.87) * mm});
            skLineSegment(sketch, "E10.36.1", {"start": v(116.94, -27.4) * mm, "end": v(116.03, -29.8) * mm});
            skPoint(sketch, "E10.36.2", {"position": v(125.77, -24) * mm});
            skLineSegment(sketch, "E10.36.3", {"start": v(123.28, -26.37) * mm, "end": v(116.94, -27.4) * mm});
            skLineSegment(sketch, "E10.36.4", {"start": v(118.81, -17.58) * mm, "end": v(118.85, -15.01) * mm});
            skLineSegment(sketch, "E10.36.5", {"start": v(118.81, -17.58) * mm, "end": v(124.33, -20.87) * mm});
            skLineSegment(sketch, "E10.36.6", {"start": v(124.33, -20.87) * mm, "end": v(123.28, -26.37) * mm, "construction": true});
            skArc(sketch, "E10.37.0", {"start": v(125.61, -10.71) * mm, "mid": v(127.79, -8.04) * mm, "end": v(125.97, -5.12) * mm});
            skLineSegment(sketch, "E10.37.1", {"start": v(119.45, -12.53) * mm, "end": v(118.85, -15.01) * mm});
            skPoint(sketch, "E10.37.2", {"position": v(127.79, -8.04) * mm});
            skLineSegment(sketch, "E10.37.3", {"start": v(125.61, -10.71) * mm, "end": v(119.45, -12.53) * mm});
            skLineSegment(sketch, "E10.37.4", {"start": v(120.08, -2.55) * mm, "end": v(119.8, 0) * mm});
            skLineSegment(sketch, "E10.37.5", {"start": v(120.08, -2.55) * mm, "end": v(125.97, -5.12) * mm});
            skLineSegment(sketch, "E10.37.6", {"start": v(125.97, -5.12) * mm, "end": v(125.61, -10.71) * mm, "construction": true});
            skArc(sketch, "E10.38.0", {"start": v(125.97, 5.12) * mm, "mid": v(127.79, 8.04) * mm, "end": v(125.61, 10.71) * mm});
            skLineSegment(sketch, "E10.38.1", {"start": v(120.08, 2.54) * mm, "end": v(119.8, 0) * mm});
            skPoint(sketch, "E10.38.2", {"position": v(127.79, 8.04) * mm});
            skLineSegment(sketch, "E10.38.3", {"start": v(125.97, 5.12) * mm, "end": v(120.08, 2.54) * mm});
            skLineSegment(sketch, "E10.38.4", {"start": v(119.45, 12.52) * mm, "end": v(118.85, 15.01) * mm});
            skLineSegment(sketch, "E10.38.5", {"start": v(119.45, 12.52) * mm, "end": v(125.61, 10.71) * mm});
            skLineSegment(sketch, "E10.38.6", {"start": v(125.61, 10.71) * mm, "end": v(125.97, 5.12) * mm, "construction": true});
            skArc(sketch, "E10.39.0", {"start": v(124.33, 20.86) * mm, "mid": v(125.77, 24) * mm, "end": v(123.28, 26.37) * mm});
            skLineSegment(sketch, "E10.39.1", {"start": v(118.81, 17.57) * mm, "end": v(118.85, 15.01) * mm});
            skPoint(sketch, "E10.39.2", {"position": v(125.77, 24) * mm});
            skLineSegment(sketch, "E10.39.3", {"start": v(124.33, 20.86) * mm, "end": v(118.81, 17.57) * mm});
            skLineSegment(sketch, "E10.39.4", {"start": v(116.94, 27.4) * mm, "end": v(116.03, 29.8) * mm});
            skLineSegment(sketch, "E10.39.5", {"start": v(116.94, 27.4) * mm, "end": v(123.28, 26.37) * mm});
            skLineSegment(sketch, "E10.39.6", {"start": v(123.28, 26.37) * mm, "end": v(124.33, 20.86) * mm, "construction": true});
            skArc(sketch, "E10.40.0", {"start": v(120.74, 36.28) * mm, "mid": v(121.77, 39.57) * mm, "end": v(119, 41.61) * mm});
            skLineSegment(sketch, "E10.40.1", {"start": v(115.67, 32.33) * mm, "end": v(116.03, 29.8) * mm});
            skPoint(sketch, "E10.40.2", {"position": v(121.77, 39.57) * mm});
            skLineSegment(sketch, "E10.40.3", {"start": v(120.74, 36.28) * mm, "end": v(115.67, 32.33) * mm});
            skLineSegment(sketch, "E10.40.4", {"start": v(112.58, 41.84) * mm, "end": v(111.38, 44.1) * mm});
            skLineSegment(sketch, "E10.40.5", {"start": v(112.58, 41.84) * mm, "end": v(119, 41.61) * mm});
            skLineSegment(sketch, "E10.40.6", {"start": v(119, 41.61) * mm, "end": v(120.74, 36.28) * mm, "construction": true});
            skArc(sketch, "E10.41.0", {"start": v(115.24, 51.13) * mm, "mid": v(115.85, 54.52) * mm, "end": v(112.85, 56.2) * mm});
            skLineSegment(sketch, "E10.41.1", {"start": v(110.7, 46.57) * mm, "end": v(111.38, 44.1) * mm});
            skPoint(sketch, "E10.41.2", {"position": v(115.85, 54.52) * mm});
            skLineSegment(sketch, "E10.41.3", {"start": v(115.24, 51.13) * mm, "end": v(110.7, 46.57) * mm});
            skLineSegment(sketch, "E10.41.4", {"start": v(106.45, 55.62) * mm, "end": v(104.97, 57.7) * mm});
            skLineSegment(sketch, "E10.41.5", {"start": v(106.45, 55.62) * mm, "end": v(112.85, 56.2) * mm});
            skLineSegment(sketch, "E10.41.6", {"start": v(112.85, 56.2) * mm, "end": v(115.24, 51.13) * mm, "construction": true});
            skArc(sketch, "E10.42.0", {"start": v(107.92, 65.17) * mm, "mid": v(108.1, 68.6) * mm, "end": v(104.92, 69.9) * mm});
            skLineSegment(sketch, "E10.42.1", {"start": v(104, 60.08) * mm, "end": v(104.97, 57.7) * mm});
            skPoint(sketch, "E10.42.2", {"position": v(108.1, 68.6) * mm});
            skLineSegment(sketch, "E10.42.3", {"start": v(107.92, 65.17) * mm, "end": v(104, 60.08) * mm});
            skLineSegment(sketch, "E10.42.4", {"start": v(98.64, 68.52) * mm, "end": v(96.91, 70.41) * mm});
            skLineSegment(sketch, "E10.42.5", {"start": v(98.64, 68.52) * mm, "end": v(104.92, 69.9) * mm});
            skLineSegment(sketch, "E10.42.6", {"start": v(104.92, 69.9) * mm, "end": v(107.92, 65.17) * mm, "construction": true});
            skArc(sketch, "E10.43.0", {"start": v(98.9, 78.18) * mm, "mid": v(98.66, 81.61) * mm, "end": v(95.33, 82.5) * mm});
            skLineSegment(sketch, "E10.43.1", {"start": v(95.65, 72.64) * mm, "end": v(96.91, 70.41) * mm});
            skPoint(sketch, "E10.43.2", {"position": v(98.66, 81.61) * mm});
            skLineSegment(sketch, "E10.43.3", {"start": v(98.9, 78.18) * mm, "end": v(95.65, 72.64) * mm});
            skLineSegment(sketch, "E10.43.4", {"start": v(89.27, 80.34) * mm, "end": v(87.32, 82) * mm});
            skLineSegment(sketch, "E10.43.5", {"start": v(89.27, 80.34) * mm, "end": v(95.33, 82.5) * mm});
            skLineSegment(sketch, "E10.43.6", {"start": v(95.33, 82.5) * mm, "end": v(98.9, 78.18) * mm, "construction": true});
            skArc(sketch, "E10.44.0", {"start": v(88.32, 89.96) * mm, "mid": v(87.65, 93.34) * mm, "end": v(84.24, 93.8) * mm});
            skLineSegment(sketch, "E10.44.1", {"start": v(85.8, 84.05) * mm, "end": v(87.32, 82) * mm});
            skPoint(sketch, "E10.44.2", {"position": v(87.65, 93.34) * mm});
            skLineSegment(sketch, "E10.44.3", {"start": v(88.32, 89.96) * mm, "end": v(85.8, 84.05) * mm});
            skLineSegment(sketch, "E10.44.4", {"start": v(78.5, 90.9) * mm, "end": v(76.36, 92.3) * mm});
            skLineSegment(sketch, "E10.44.5", {"start": v(78.5, 90.9) * mm, "end": v(84.24, 93.8) * mm});
            skLineSegment(sketch, "E10.44.6", {"start": v(84.24, 93.8) * mm, "end": v(88.32, 89.96) * mm, "construction": true});
            skArc(sketch, "E10.45.0", {"start": v(76.35, 100.32) * mm, "mid": v(75.26, 103.58) * mm, "end": v(71.82, 103.61) * mm});
            skLineSegment(sketch, "E10.45.1", {"start": v(74.58, 94.14) * mm, "end": v(76.36, 92.3) * mm});
            skPoint(sketch, "E10.45.2", {"position": v(75.26, 103.58) * mm});
            skLineSegment(sketch, "E10.45.3", {"start": v(76.35, 100.32) * mm, "end": v(74.58, 94.14) * mm});
            skLineSegment(sketch, "E10.45.4", {"start": v(66.49, 100.02) * mm, "end": v(64.19, 101.14) * mm});
            skLineSegment(sketch, "E10.45.5", {"start": v(66.49, 100.02) * mm, "end": v(71.82, 103.61) * mm});
            skLineSegment(sketch, "E10.45.6", {"start": v(71.82, 103.61) * mm, "end": v(76.35, 100.32) * mm, "construction": true});
            skArc(sketch, "E10.46.0", {"start": v(63.18, 109.1) * mm, "mid": v(61.68, 112.2) * mm, "end": v(58.26, 111.8) * mm});
            skLineSegment(sketch, "E10.46.1", {"start": v(62.2, 102.75) * mm, "end": v(64.19, 101.14) * mm});
            skPoint(sketch, "E10.46.2", {"position": v(61.68, 112.2) * mm});
            skLineSegment(sketch, "E10.46.3", {"start": v(63.18, 109.1) * mm, "end": v(62.2, 102.75) * mm});
            skLineSegment(sketch, "E10.46.4", {"start": v(53.43, 107.57) * mm, "end": v(51, 108.4) * mm});
            skLineSegment(sketch, "E10.46.5", {"start": v(53.43, 107.57) * mm, "end": v(58.26, 111.8) * mm});
            skLineSegment(sketch, "E10.46.6", {"start": v(58.26, 111.8) * mm, "end": v(63.18, 109.1) * mm, "construction": true});
            skArc(sketch, "E10.47.0", {"start": v(49, 116.16) * mm, "mid": v(47.13, 119.05) * mm, "end": v(43.8, 118.22) * mm});
            skLineSegment(sketch, "E10.47.1", {"start": v(48.82, 109.73) * mm, "end": v(51, 108.4) * mm});
            skPoint(sketch, "E10.47.2", {"position": v(47.13, 119.05) * mm});
            skLineSegment(sketch, "E10.47.3", {"start": v(49, 116.16) * mm, "end": v(48.82, 109.73) * mm});
            skLineSegment(sketch, "E10.47.4", {"start": v(39.53, 113.41) * mm, "end": v(37.02, 113.93) * mm});
            skLineSegment(sketch, "E10.47.5", {"start": v(39.53, 113.41) * mm, "end": v(43.8, 118.22) * mm});
            skLineSegment(sketch, "E10.47.6", {"start": v(43.8, 118.22) * mm, "end": v(49, 116.16) * mm, "construction": true});
            skArc(sketch, "E10.48.0", {"start": v(34.06, 121.38) * mm, "mid": v(31.84, 124.02) * mm, "end": v(28.63, 122.78) * mm});
            skLineSegment(sketch, "E10.48.1", {"start": v(34.69, 114.99) * mm, "end": v(37.02, 113.93) * mm});
            skPoint(sketch, "E10.48.2", {"position": v(31.84, 124.02) * mm});
            skLineSegment(sketch, "E10.48.3", {"start": v(34.06, 121.38) * mm, "end": v(34.69, 114.99) * mm});
            skLineSegment(sketch, "E10.48.4", {"start": v(25, 117.47) * mm, "end": v(22.45, 117.67) * mm});
            skLineSegment(sketch, "E10.48.5", {"start": v(25, 117.47) * mm, "end": v(28.63, 122.78) * mm});
            skLineSegment(sketch, "E10.48.6", {"start": v(28.63, 122.78) * mm, "end": v(34.06, 121.38) * mm, "construction": true});
            skArc(sketch, "E10.49.0", {"start": v(18.58, 124.7) * mm, "mid": v(16.05, 127.03) * mm, "end": v(13.02, 125.4) * mm});
            skLineSegment(sketch, "E10.49.1", {"start": v(20, 118.43) * mm, "end": v(22.45, 117.67) * mm});
            skPoint(sketch, "E10.49.2", {"position": v(16.05, 127.03) * mm});
            skLineSegment(sketch, "E10.49.3", {"start": v(18.58, 124.7) * mm, "end": v(20, 118.43) * mm});
            skLineSegment(sketch, "E10.49.4", {"start": v(10.08, 119.68) * mm, "end": v(7.52, 119.56) * mm});
            skLineSegment(sketch, "E10.49.5", {"start": v(10.08, 119.68) * mm, "end": v(13.02, 125.4) * mm});
            skLineSegment(sketch, "E10.49.6", {"start": v(13.02, 125.4) * mm, "end": v(18.58, 124.7) * mm, "construction": true});
            skPoint(sketch, "E10.center", {"position": v(0, 0) * mm});
            skSolve(sketch);
        }
        {
            var Q0;
            Q0 = qSketchRegion(id + "F6", true);
            extrude(context, id + "F7", {"entities" : qUnion([Q0]), "operationType" : NewBodyOperationType.ADD, "oppositeDirection" : true, "depth" : 5 * mm, "offsetDistance" : 25 * mm});
        }
        {
            var Q0;
            Q0=makeQuery(id+"F7.opExtrude","CAP_EDGE",EDGE,{"disambiguationData":[OSD([sQuery(id+"F6.wireOp",EDGE,"E10.3.5")])],"isStart":true});
            var Q1;
            Q1=makeQuery(id+"F7.opExtrude","CAP_EDGE",EDGE,{"disambiguationData":[OSD([sQuery(id+"F6.wireOp",EDGE,"E10.2.5")])],"isStart":true});
            var Q2;
            Q2=makeQuery(id+"F7.opExtrude","CAP_EDGE",EDGE,{"disambiguationData":[OSD([sQuery(id+"F6.wireOp",EDGE,"E6")])],"isStart":true});
            var Q3;
            Q3=makeQuery(id+"F7.opExtrude","CAP_EDGE",EDGE,{"disambiguationData":[OSD([sQuery(id+"F6.wireOp",EDGE,"E10.10.0")])],"isStart":true});
            var Q4;
            Q4=makeQuery(id+"F7.opExtrude","CAP_EDGE",EDGE,{"disambiguationData":[OSD([sQuery(id+"F6.wireOp",EDGE,"E10.18.0")])],"isStart":true});
            var Q5;
            Q5=makeQuery(id+"F7.opExtrude","CAP_EDGE",EDGE,{"disambiguationData":[OSD([sQuery(id+"F6.wireOp",EDGE,"E10.7.0")])],"isStart":true});
            var Q6;
            Q6=makeQuery(id+"F7.opExtrude","CAP_EDGE",EDGE,{"disambiguationData":[OSD([sQuery(id+"F6.wireOp",EDGE,"E10.15.0")])],"isStart":true});
            var Q7;
            Q7=makeQuery(id+"F7.opExtrude","CAP_EDGE",EDGE,{"disambiguationData":[OSD([sQuery(id+"F6.wireOp",EDGE,"E10.23.0")])],"isStart":true});
            var Q8;
            Q8=makeQuery(id+"F7.opExtrude","CAP_EDGE",EDGE,{"disambiguationData":[OSD([sQuery(id+"F6.wireOp",EDGE,"E10.4.0")])],"isStart":true});
            var Q9;
            Q9=makeQuery(id+"F7.opExtrude","CAP_EDGE",EDGE,{"disambiguationData":[OSD([sQuery(id+"F6.wireOp",EDGE,"E10.12.0")])],"isStart":true});
            var Q10;
            Q10=makeQuery(id+"F7.opExtrude","CAP_EDGE",EDGE,{"disambiguationData":[OSD([sQuery(id+"F6.wireOp",EDGE,"E10.20.0")])],"isStart":true});
            var Q11;
            Q11=makeQuery(id+"F7.opExtrude","CAP_EDGE",EDGE,{"disambiguationData":[OSD([sQuery(id+"F6.wireOp",EDGE,"E10.1.0")])],"isStart":true});
            var Q12;
            Q12=makeQuery(id+"F7.opExtrude","CAP_EDGE",EDGE,{"disambiguationData":[OSD([sQuery(id+"F6.wireOp",EDGE,"E10.9.0")])],"isStart":true});
            var Q13;
            Q13=makeQuery(id+"F7.opExtrude","CAP_EDGE",EDGE,{"disambiguationData":[OSD([sQuery(id+"F6.wireOp",EDGE,"E10.17.0")])],"isStart":true});
            var Q14;
            Q14=makeQuery(id+"F7.opExtrude","CAP_EDGE",EDGE,{"disambiguationData":[OSD([sQuery(id+"F6.wireOp",EDGE,"E10.25.0")])],"isStart":true});
            var Q15;
            Q15=makeQuery(id+"F7.opExtrude","CAP_EDGE",EDGE,{"disambiguationData":[OSD([sQuery(id+"F6.wireOp",EDGE,"E10.6.0")])],"isStart":true});
            var Q16;
            Q16=makeQuery(id+"F7.opExtrude","CAP_EDGE",EDGE,{"disambiguationData":[OSD([sQuery(id+"F6.wireOp",EDGE,"E10.14.0")])],"isStart":true});
            var Q17;
            Q17=makeQuery(id+"F7.opExtrude","CAP_EDGE",EDGE,{"disambiguationData":[OSD([sQuery(id+"F6.wireOp",EDGE,"E10.22.0")])],"isStart":true});
            var Q18;
            Q18=makeQuery(id+"F7.opExtrude","CAP_EDGE",EDGE,{"disambiguationData":[OSD([sQuery(id+"F6.wireOp",EDGE,"E10.3.0")])],"isStart":true});
            var Q19;
            Q19=makeQuery(id+"F7.opExtrude","CAP_EDGE",EDGE,{"disambiguationData":[OSD([sQuery(id+"F6.wireOp",EDGE,"E10.11.0")])],"isStart":true});
            var Q20;
            Q20=makeQuery(id+"F7.opExtrude","CAP_EDGE",EDGE,{"disambiguationData":[OSD([sQuery(id+"F6.wireOp",EDGE,"E10.19.0")])],"isStart":true});
            var Q21;
            Q21=makeQuery(id+"F7.opExtrude","CAP_EDGE",EDGE,{"disambiguationData":[OSD([sQuery(id+"F6.wireOp",EDGE,"E10.8.0")])],"isStart":true});
            var Q22;
            Q22=makeQuery(id+"F7.opExtrude","CAP_EDGE",EDGE,{"disambiguationData":[OSD([sQuery(id+"F6.wireOp",EDGE,"E10.16.0")])],"isStart":true});
            var Q23;
            Q23=makeQuery(id+"F7.opExtrude","CAP_EDGE",EDGE,{"disambiguationData":[OSD([sQuery(id+"F6.wireOp",EDGE,"E10.24.0")])],"isStart":true});
            var Q24;
            Q24=makeQuery(id+"F7.opExtrude","CAP_EDGE",EDGE,{"disambiguationData":[OSD([sQuery(id+"F6.wireOp",EDGE,"E10.5.0")])],"isStart":true});
            var Q25;
            Q25=makeQuery(id+"F7.opExtrude","CAP_EDGE",EDGE,{"disambiguationData":[OSD([sQuery(id+"F6.wireOp",EDGE,"E10.13.0")])],"isStart":true});
            var Q26;
            Q26=makeQuery(id+"F7.opExtrude","CAP_EDGE",EDGE,{"disambiguationData":[OSD([sQuery(id+"F6.wireOp",EDGE,"E10.21.0")])],"isStart":true});
            var Q27;
            {var subQ0=sQuery(id+"F6.wireOp",EDGE,"E10.14.5");var subQ2=sQuery(id+"F0.wireOp",EDGE,"E0");Q27=makeQuery(id+"F7.boolean.opBoolean","SPLIT",EDGE,{"disambiguationData":[TD([makeQuery(id+"F7.opExtrude","SWEPT_FACE",FACE,{"disambiguationData":[OSD([subQ0])]})])],"derivedFrom":makeQuery(id+"F1.opExtrude","CAP_EDGE",EDGE,{"disambiguationData":[OSD([subQ2])],"isStart":false})});}
            var Q28;
            Q28=makeQuery(id+"F7.opExtrude","CAP_EDGE",EDGE,{"disambiguationData":[OSD([sQuery(id+"F6.wireOp",EDGE,"E10.7.5")])],"isStart":true});
            var Q29;
            Q29=makeQuery(id+"F7.opExtrude","CAP_EDGE",EDGE,{"disambiguationData":[OSD([sQuery(id+"F6.wireOp",EDGE,"E10.11.5")])],"isStart":true});
            var Q30;
            {var subQ0=sQuery(id+"F6.wireOp",EDGE,"E10.15.5");var subQ2=sQuery(id+"F0.wireOp",EDGE,"E0");Q30=makeQuery(id+"F7.boolean.opBoolean","SPLIT",EDGE,{"disambiguationData":[TD([makeQuery(id+"F7.opExtrude","SWEPT_FACE",FACE,{"disambiguationData":[OSD([subQ0])]})])],"derivedFrom":makeQuery(id+"F1.opExtrude","CAP_EDGE",EDGE,{"disambiguationData":[OSD([subQ2])],"isStart":false})});}
            var Q31;
            {var subQ0=sQuery(id+"F6.wireOp",EDGE,"E10.16.5");var subQ2=sQuery(id+"F0.wireOp",EDGE,"E0");Q31=makeQuery(id+"F7.boolean.opBoolean","SPLIT",EDGE,{"disambiguationData":[TD([makeQuery(id+"F7.opExtrude","SWEPT_FACE",FACE,{"disambiguationData":[OSD([subQ0])]})])],"derivedFrom":makeQuery(id+"F1.opExtrude","CAP_EDGE",EDGE,{"disambiguationData":[OSD([subQ2])],"isStart":false})});}
            var Q32;
            Q32=makeQuery(id+"F7.opExtrude","CAP_EDGE",EDGE,{"disambiguationData":[OSD([sQuery(id+"F6.wireOp",EDGE,"E10.4.5")])],"isStart":true});
            var Q33;
            Q33=makeQuery(id+"F7.opExtrude","CAP_EDGE",EDGE,{"disambiguationData":[OSD([sQuery(id+"F6.wireOp",EDGE,"E10.17.3")])],"isStart":true});
            var Q34;
            Q34=makeQuery(id+"F7.opExtrude","CAP_EDGE",EDGE,{"disambiguationData":[OSD([sQuery(id+"F6.wireOp",EDGE,"E10.21.3")])],"isStart":true});
            var Q35;
            Q35=makeQuery(id+"F7.opExtrude","CAP_EDGE",EDGE,{"disambiguationData":[OSD([sQuery(id+"F6.wireOp",EDGE,"E10.5.5")])],"isStart":true});
            var Q36;
            Q36=makeQuery(id+"F7.opExtrude","CAP_EDGE",EDGE,{"disambiguationData":[OSD([sQuery(id+"F6.wireOp",EDGE,"E10.9.5")])],"isStart":true});
            var Q37;
            Q37=makeQuery(id+"F7.opExtrude","CAP_EDGE",EDGE,{"disambiguationData":[OSD([sQuery(id+"F6.wireOp",EDGE,"E10.14.3")])],"isStart":true});
            var Q38;
            Q38=makeQuery(id+"F7.opExtrude","CAP_EDGE",EDGE,{"disambiguationData":[OSD([sQuery(id+"F6.wireOp",EDGE,"E10.18.3")])],"isStart":true});
            var Q39;
            Q39=makeQuery(id+"F7.opExtrude","CAP_EDGE",EDGE,{"disambiguationData":[OSD([sQuery(id+"F6.wireOp",EDGE,"E10.22.3")])],"isStart":true});
            var Q40;
            {var subQ0=sQuery(id+"F6.wireOp",EDGE,"E10.10.5");var subQ2=sQuery(id+"F0.wireOp",EDGE,"E0");Q40=makeQuery(id+"F7.boolean.opBoolean","SPLIT",EDGE,{"disambiguationData":[TD([makeQuery(id+"F7.opExtrude","SWEPT_FACE",FACE,{"disambiguationData":[OSD([subQ0])]})])],"derivedFrom":makeQuery(id+"F1.opExtrude","CAP_EDGE",EDGE,{"disambiguationData":[OSD([subQ2])],"isStart":false})});}
            var Q41;
            Q41=makeQuery(id+"F7.opExtrude","CAP_EDGE",EDGE,{"disambiguationData":[OSD([sQuery(id+"F6.wireOp",EDGE,"E10.6.5")])],"isStart":true});
            var Q42;
            {var subQ0=sQuery(id+"F6.wireOp",EDGE,"E10.11.5");var subQ2=sQuery(id+"F0.wireOp",EDGE,"E0");Q42=makeQuery(id+"F7.boolean.opBoolean","SPLIT",EDGE,{"disambiguationData":[TD([makeQuery(id+"F7.opExtrude","SWEPT_FACE",FACE,{"disambiguationData":[OSD([subQ0])]})])],"derivedFrom":makeQuery(id+"F1.opExtrude","CAP_EDGE",EDGE,{"disambiguationData":[OSD([subQ2])],"isStart":false})});}
            var Q43;
            {var subQ0=sQuery(id+"F6.wireOp",EDGE,"E10.12.5");var subQ2=sQuery(id+"F0.wireOp",EDGE,"E0");Q43=makeQuery(id+"F7.boolean.opBoolean","SPLIT",EDGE,{"disambiguationData":[TD([makeQuery(id+"F7.opExtrude","SWEPT_FACE",FACE,{"disambiguationData":[OSD([subQ0])]})])],"derivedFrom":makeQuery(id+"F1.opExtrude","CAP_EDGE",EDGE,{"disambiguationData":[OSD([subQ2])],"isStart":false})});}
            var Q44;
            Q44=makeQuery(id+"F7.opExtrude","CAP_EDGE",EDGE,{"disambiguationData":[OSD([sQuery(id+"F6.wireOp",EDGE,"E10.19.3")])],"isStart":true});
            var Q45;
            {var subQ0=sQuery(id+"F6.wireOp",EDGE,"E10.13.5");var subQ1=sQuery(id+"F0.wireOp",EDGE,"E0");Q45=makeQuery(id+"F7.boolean.opBoolean","SPLIT",EDGE,{"disambiguationData":[TD([makeQuery(id+"F7.opExtrude","SWEPT_FACE",FACE,{"disambiguationData":[OSD([subQ0])]})])],"derivedFrom":makeQuery(id+"F1.opExtrude","CAP_EDGE",EDGE,{"disambiguationData":[OSD([subQ1])],"isStart":false})});}
            var Q46;
            Q46=makeQuery(id+"F7.opExtrude","CAP_EDGE",EDGE,{"disambiguationData":[OSD([sQuery(id+"F6.wireOp",EDGE,"E3")])],"isStart":true});
            var Q47;
            Q47=makeQuery(id+"F7.opExtrude","CAP_EDGE",EDGE,{"disambiguationData":[OSD([sQuery(id+"F6.wireOp",EDGE,"E10.1.3")])],"isStart":true});
            var Q48;
            Q48=makeQuery(id+"F7.opExtrude","CAP_EDGE",EDGE,{"disambiguationData":[OSD([sQuery(id+"F6.wireOp",EDGE,"E10.1.5")])],"isStart":true});
            var Q49;
            Q49=makeQuery(id+"F7.opExtrude","CAP_EDGE",EDGE,{"disambiguationData":[OSD([sQuery(id+"F6.wireOp",EDGE,"E10.2.3")])],"isStart":true});
            var Q50;
            Q50=makeQuery(id+"F7.opExtrude","CAP_EDGE",EDGE,{"disambiguationData":[OSD([sQuery(id+"F6.wireOp",EDGE,"E10.3.3")])],"isStart":true});
            var Q51;
            Q51=makeQuery(id+"F7.opExtrude","CAP_EDGE",EDGE,{"disambiguationData":[OSD([sQuery(id+"F6.wireOp",EDGE,"E10.2.0")])],"isStart":true});
            var Q52;
            Q52=makeQuery(id+"F7.opExtrude","CAP_EDGE",EDGE,{"disambiguationData":[OSD([sQuery(id+"F6.wireOp",EDGE,"E10.34.0")])],"isStart":true});
            var Q53;
            Q53=makeQuery(id+"F7.opExtrude","CAP_EDGE",EDGE,{"disambiguationData":[OSD([sQuery(id+"F6.wireOp",EDGE,"E10.39.0")])],"isStart":true});
            var Q54;
            Q54=makeQuery(id+"F7.opExtrude","CAP_EDGE",EDGE,{"disambiguationData":[OSD([sQuery(id+"F6.wireOp",EDGE,"E10.36.0")])],"isStart":true});
            var Q55;
            Q55=makeQuery(id+"F7.opExtrude","CAP_EDGE",EDGE,{"disambiguationData":[OSD([sQuery(id+"F6.wireOp",EDGE,"E10.33.0")])],"isStart":true});
            var Q56;
            Q56=makeQuery(id+"F7.opExtrude","CAP_EDGE",EDGE,{"disambiguationData":[OSD([sQuery(id+"F6.wireOp",EDGE,"E10.41.0")])],"isStart":true});
            var Q57;
            Q57=makeQuery(id+"F7.opExtrude","CAP_EDGE",EDGE,{"disambiguationData":[OSD([sQuery(id+"F6.wireOp",EDGE,"E10.35.0")])],"isStart":true});
            var Q58;
            Q58=makeQuery(id+"F7.opExtrude","CAP_EDGE",EDGE,{"disambiguationData":[OSD([sQuery(id+"F6.wireOp",EDGE,"E10.40.0")])],"isStart":true});
            var Q59;
            Q59=makeQuery(id+"F7.opExtrude","CAP_EDGE",EDGE,{"disambiguationData":[OSD([sQuery(id+"F6.wireOp",EDGE,"E10.15.5")])],"isStart":true});
            var Q60;
            Q60=makeQuery(id+"F7.opExtrude","CAP_EDGE",EDGE,{"disambiguationData":[OSD([sQuery(id+"F6.wireOp",EDGE,"E10.19.5")])],"isStart":true});
            var Q61;
            Q61=makeQuery(id+"F7.opExtrude","CAP_EDGE",EDGE,{"disambiguationData":[OSD([sQuery(id+"F6.wireOp",EDGE,"E10.23.5")])],"isStart":true});
            var Q62;
            Q62=makeQuery(id+"F7.opExtrude","CAP_EDGE",EDGE,{"disambiguationData":[OSD([sQuery(id+"F6.wireOp",EDGE,"E10.31.5")])],"isStart":true});
            var Q63;
            Q63=makeQuery(id+"F7.opExtrude","CAP_EDGE",EDGE,{"disambiguationData":[OSD([sQuery(id+"F6.wireOp",EDGE,"E10.4.3")])],"isStart":true});
            var Q64;
            Q64=makeQuery(id+"F7.opExtrude","CAP_EDGE",EDGE,{"disambiguationData":[OSD([sQuery(id+"F6.wireOp",EDGE,"E10.8.3")])],"isStart":true});
            var Q65;
            Q65=makeQuery(id+"F7.opExtrude","CAP_EDGE",EDGE,{"disambiguationData":[OSD([sQuery(id+"F6.wireOp",EDGE,"E10.12.3")])],"isStart":true});
            var Q66;
            Q66=makeQuery(id+"F7.opExtrude","CAP_EDGE",EDGE,{"disambiguationData":[OSD([sQuery(id+"F6.wireOp",EDGE,"E10.16.3")])],"isStart":true});
            var Q67;
            Q67=makeQuery(id+"F7.opExtrude","CAP_EDGE",EDGE,{"disambiguationData":[OSD([sQuery(id+"F6.wireOp",EDGE,"E10.20.3")])],"isStart":true});
            var Q68;
            Q68=makeQuery(id+"F7.opExtrude","CAP_EDGE",EDGE,{"disambiguationData":[OSD([sQuery(id+"F6.wireOp",EDGE,"E10.24.3")])],"isStart":true});
            var Q69;
            Q69=makeQuery(id+"F7.opExtrude","CAP_EDGE",EDGE,{"disambiguationData":[OSD([sQuery(id+"F6.wireOp",EDGE,"E10.44.3")])],"isStart":true});
            var Q70;
            {var subQ0=sQuery(id+"F6.wireOp",EDGE,"E10.17.5");var subQ1=sQuery(id+"F0.wireOp",EDGE,"E0");Q70=makeQuery(id+"F7.boolean.opBoolean","SPLIT",EDGE,{"disambiguationData":[TD([makeQuery(id+"F7.opExtrude","SWEPT_FACE",FACE,{"disambiguationData":[OSD([subQ0])]})])],"derivedFrom":makeQuery(id+"F1.opExtrude","CAP_EDGE",EDGE,{"disambiguationData":[OSD([subQ1])],"isStart":false})});}
            var Q71;
            {var subQ0=sQuery(id+"F6.wireOp",EDGE,"E10.33.5");var subQ2=sQuery(id+"F0.wireOp",EDGE,"E0");Q71=makeQuery(id+"F7.boolean.opBoolean","SPLIT",EDGE,{"disambiguationData":[TD([makeQuery(id+"F7.opExtrude","SWEPT_FACE",FACE,{"disambiguationData":[OSD([subQ0])]})])],"derivedFrom":makeQuery(id+"F1.opExtrude","CAP_EDGE",EDGE,{"disambiguationData":[OSD([subQ2])],"isStart":false})});}
            var Q72;
            {var subQ0=sQuery(id+"F6.wireOp",EDGE,"E10.18.5");var subQ2=sQuery(id+"F0.wireOp",EDGE,"E0");Q72=makeQuery(id+"F7.boolean.opBoolean","SPLIT",EDGE,{"disambiguationData":[TD([makeQuery(id+"F7.opExtrude","SWEPT_FACE",FACE,{"disambiguationData":[OSD([subQ0])]})])],"derivedFrom":makeQuery(id+"F1.opExtrude","CAP_EDGE",EDGE,{"disambiguationData":[OSD([subQ2])],"isStart":false})});}
            var Q73;
            {var subQ0=sQuery(id+"F6.wireOp",EDGE,"E10.34.5");var subQ2=sQuery(id+"F0.wireOp",EDGE,"E0");Q73=makeQuery(id+"F7.boolean.opBoolean","SPLIT",EDGE,{"disambiguationData":[TD([makeQuery(id+"F7.opExtrude","SWEPT_FACE",FACE,{"disambiguationData":[OSD([subQ0])]})])],"derivedFrom":makeQuery(id+"F1.opExtrude","CAP_EDGE",EDGE,{"disambiguationData":[OSD([subQ2])],"isStart":false})});}
            var Q74;
            Q74=makeQuery(id+"F7.opExtrude","CAP_EDGE",EDGE,{"disambiguationData":[OSD([sQuery(id+"F6.wireOp",EDGE,"E10.8.5")])],"isStart":true});
            var Q75;
            Q75=makeQuery(id+"F7.opExtrude","CAP_EDGE",EDGE,{"disambiguationData":[OSD([sQuery(id+"F6.wireOp",EDGE,"E10.12.5")])],"isStart":true});
            var Q76;
            Q76=makeQuery(id+"F7.opExtrude","CAP_EDGE",EDGE,{"disambiguationData":[OSD([sQuery(id+"F6.wireOp",EDGE,"E10.16.5")])],"isStart":true});
            var Q77;
            Q77=makeQuery(id+"F7.opExtrude","CAP_EDGE",EDGE,{"disambiguationData":[OSD([sQuery(id+"F6.wireOp",EDGE,"E10.20.5")])],"isStart":true});
            var Q78;
            Q78=makeQuery(id+"F7.opExtrude","CAP_EDGE",EDGE,{"disambiguationData":[OSD([sQuery(id+"F6.wireOp",EDGE,"E10.24.5")])],"isStart":true});
            var Q79;
            Q79=makeQuery(id+"F7.opExtrude","CAP_EDGE",EDGE,{"disambiguationData":[OSD([sQuery(id+"F6.wireOp",EDGE,"E10.32.5")])],"isStart":true});
            var Q80;
            {var subQ0=sQuery(id+"F6.wireOp",EDGE,"E10.35.5");var subQ1=sQuery(id+"F0.wireOp",EDGE,"E0");Q80=makeQuery(id+"F7.boolean.opBoolean","SPLIT",EDGE,{"disambiguationData":[TD([makeQuery(id+"F7.opExtrude","SWEPT_FACE",FACE,{"disambiguationData":[OSD([subQ0])]})])],"derivedFrom":makeQuery(id+"F1.opExtrude","CAP_EDGE",EDGE,{"disambiguationData":[OSD([subQ1])],"isStart":false})});}
            var Q81;
            Q81=makeQuery(id+"F7.opExtrude","CAP_EDGE",EDGE,{"disambiguationData":[OSD([sQuery(id+"F6.wireOp",EDGE,"E10.5.3")])],"isStart":true});
            var Q82;
            Q82=makeQuery(id+"F7.opExtrude","CAP_EDGE",EDGE,{"disambiguationData":[OSD([sQuery(id+"F6.wireOp",EDGE,"E10.9.3")])],"isStart":true});
            var Q83;
            Q83=makeQuery(id+"F7.opExtrude","CAP_EDGE",EDGE,{"disambiguationData":[OSD([sQuery(id+"F6.wireOp",EDGE,"E10.13.3")])],"isStart":true});
            var Q84;
            Q84=makeQuery(id+"F7.opExtrude","CAP_EDGE",EDGE,{"disambiguationData":[OSD([sQuery(id+"F6.wireOp",EDGE,"E10.41.3")])],"isStart":true});
            var Q85;
            Q85=makeQuery(id+"F7.opExtrude","CAP_EDGE",EDGE,{"disambiguationData":[OSD([sQuery(id+"F6.wireOp",EDGE,"E10.45.3")])],"isStart":true});
            var Q86;
            {var subQ0=sQuery(id+"F6.wireOp",EDGE,"E10.5.5");var subQ2=sQuery(id+"F0.wireOp",EDGE,"E0");Q86=makeQuery(id+"F7.boolean.opBoolean","SPLIT",EDGE,{"disambiguationData":[TD([makeQuery(id+"F7.opExtrude","SWEPT_FACE",FACE,{"disambiguationData":[OSD([subQ0])]})])],"derivedFrom":makeQuery(id+"F1.opExtrude","CAP_EDGE",EDGE,{"disambiguationData":[OSD([subQ2])],"isStart":false})});}
            var Q87;
            {var subQ0=sQuery(id+"F6.wireOp",EDGE,"E10.21.5");var subQ2=sQuery(id+"F0.wireOp",EDGE,"E0");Q87=makeQuery(id+"F7.boolean.opBoolean","SPLIT",EDGE,{"disambiguationData":[TD([makeQuery(id+"F7.opExtrude","SWEPT_FACE",FACE,{"disambiguationData":[OSD([subQ0])]})])],"derivedFrom":makeQuery(id+"F1.opExtrude","CAP_EDGE",EDGE,{"disambiguationData":[OSD([subQ2])],"isStart":false})});}
            var Q88;
            {var subQ0=sQuery(id+"F6.wireOp",EDGE,"E10.6.5");var subQ1=sQuery(id+"F0.wireOp",EDGE,"E0");Q88=makeQuery(id+"F7.boolean.opBoolean","SPLIT",EDGE,{"disambiguationData":[TD([makeQuery(id+"F7.opExtrude","SWEPT_FACE",FACE,{"disambiguationData":[OSD([subQ0])]})])],"derivedFrom":makeQuery(id+"F1.opExtrude","CAP_EDGE",EDGE,{"disambiguationData":[OSD([subQ1])],"isStart":false})});}
            var Q89;
            {var subQ0=sQuery(id+"F6.wireOp",EDGE,"E10.22.5");var subQ2=sQuery(id+"F0.wireOp",EDGE,"E0");Q89=makeQuery(id+"F7.boolean.opBoolean","SPLIT",EDGE,{"disambiguationData":[TD([makeQuery(id+"F7.opExtrude","SWEPT_FACE",FACE,{"disambiguationData":[OSD([subQ0])]})])],"derivedFrom":makeQuery(id+"F1.opExtrude","CAP_EDGE",EDGE,{"disambiguationData":[OSD([subQ2])],"isStart":false})});}
            var Q90;
            Q90=makeQuery(id+"F7.opExtrude","CAP_EDGE",EDGE,{"disambiguationData":[OSD([sQuery(id+"F6.wireOp",EDGE,"E10.13.5")])],"isStart":true});
            var Q91;
            Q91=makeQuery(id+"F7.opExtrude","CAP_EDGE",EDGE,{"disambiguationData":[OSD([sQuery(id+"F6.wireOp",EDGE,"E10.17.5")])],"isStart":true});
            var Q92;
            Q92=makeQuery(id+"F7.opExtrude","CAP_EDGE",EDGE,{"disambiguationData":[OSD([sQuery(id+"F6.wireOp",EDGE,"E10.21.5")])],"isStart":true});
            var Q93;
            Q93=makeQuery(id+"F7.opExtrude","CAP_EDGE",EDGE,{"disambiguationData":[OSD([sQuery(id+"F6.wireOp",EDGE,"E10.29.5")])],"isStart":true});
            var Q94;
            Q94=makeQuery(id+"F7.opExtrude","CAP_EDGE",EDGE,{"disambiguationData":[OSD([sQuery(id+"F6.wireOp",EDGE,"E10.33.5")])],"isStart":true});
            var Q95;
            {var subQ0=sQuery(id+"F6.wireOp",EDGE,"E10.7.5");var subQ2=sQuery(id+"F0.wireOp",EDGE,"E0");Q95=makeQuery(id+"F7.boolean.opBoolean","SPLIT",EDGE,{"disambiguationData":[TD([makeQuery(id+"F7.opExtrude","SWEPT_FACE",FACE,{"disambiguationData":[OSD([subQ0])]})])],"derivedFrom":makeQuery(id+"F1.opExtrude","CAP_EDGE",EDGE,{"disambiguationData":[OSD([subQ2])],"isStart":false})});}
            var Q96;
            {var subQ0=sQuery(id+"F6.wireOp",EDGE,"E10.39.5");var subQ1=sQuery(id+"F0.wireOp",EDGE,"E0");Q96=makeQuery(id+"F7.boolean.opBoolean","SPLIT",EDGE,{"disambiguationData":[TD([makeQuery(id+"F7.opExtrude","SWEPT_FACE",FACE,{"disambiguationData":[OSD([subQ0])]})])],"derivedFrom":makeQuery(id+"F1.opExtrude","CAP_EDGE",EDGE,{"disambiguationData":[OSD([subQ1])],"isStart":false})});}
            var Q97;
            {var subQ0=sQuery(id+"F6.wireOp",EDGE,"E10.8.5");var subQ2=sQuery(id+"F0.wireOp",EDGE,"E0");Q97=makeQuery(id+"F7.boolean.opBoolean","SPLIT",EDGE,{"disambiguationData":[TD([makeQuery(id+"F7.opExtrude","SWEPT_FACE",FACE,{"disambiguationData":[OSD([subQ0])]})])],"derivedFrom":makeQuery(id+"F1.opExtrude","CAP_EDGE",EDGE,{"disambiguationData":[OSD([subQ2])],"isStart":false})});}
            var Q98;
            Q98=makeQuery(id+"F7.opExtrude","CAP_EDGE",EDGE,{"disambiguationData":[OSD([sQuery(id+"F6.wireOp",EDGE,"E10.6.3")])],"isStart":true});
            var Q99;
            Q99=makeQuery(id+"F7.opExtrude","CAP_EDGE",EDGE,{"disambiguationData":[OSD([sQuery(id+"F6.wireOp",EDGE,"E10.10.3")])],"isStart":true});
            var Q100;
            Q100=makeQuery(id+"F7.opExtrude","CAP_EDGE",EDGE,{"disambiguationData":[OSD([sQuery(id+"F6.wireOp",EDGE,"E10.46.3")])],"isStart":true});
            var Q101;
            {var subQ0=sQuery(id+"F6.wireOp",EDGE,"E10.9.5");var subQ2=sQuery(id+"F0.wireOp",EDGE,"E0");Q101=makeQuery(id+"F7.boolean.opBoolean","SPLIT",EDGE,{"disambiguationData":[TD([makeQuery(id+"F7.opExtrude","SWEPT_FACE",FACE,{"disambiguationData":[OSD([subQ0])]})])],"derivedFrom":makeQuery(id+"F1.opExtrude","CAP_EDGE",EDGE,{"disambiguationData":[OSD([subQ2])],"isStart":false})});}
            var Q102;
            Q102=makeQuery(id+"F7.opExtrude","CAP_EDGE",EDGE,{"disambiguationData":[OSD([sQuery(id+"F6.wireOp",EDGE,"E10.10.5")])],"isStart":true});
            var Q103;
            Q103=makeQuery(id+"F7.opExtrude","CAP_EDGE",EDGE,{"disambiguationData":[OSD([sQuery(id+"F6.wireOp",EDGE,"E10.14.5")])],"isStart":true});
            var Q104;
            Q104=makeQuery(id+"F7.opExtrude","CAP_EDGE",EDGE,{"disambiguationData":[OSD([sQuery(id+"F6.wireOp",EDGE,"E10.18.5")])],"isStart":true});
            var Q105;
            Q105=makeQuery(id+"F7.opExtrude","CAP_EDGE",EDGE,{"disambiguationData":[OSD([sQuery(id+"F6.wireOp",EDGE,"E10.22.5")])],"isStart":true});
            var Q106;
            Q106=makeQuery(id+"F7.opExtrude","CAP_EDGE",EDGE,{"disambiguationData":[OSD([sQuery(id+"F6.wireOp",EDGE,"E10.7.3")])],"isStart":true});
            var Q107;
            Q107=makeQuery(id+"F7.opExtrude","CAP_EDGE",EDGE,{"disambiguationData":[OSD([sQuery(id+"F6.wireOp",EDGE,"E10.11.3")])],"isStart":true});
            var Q108;
            Q108=makeQuery(id+"F7.opExtrude","CAP_EDGE",EDGE,{"disambiguationData":[OSD([sQuery(id+"F6.wireOp",EDGE,"E10.15.3")])],"isStart":true});
            var Q109;
            Q109=makeQuery(id+"F7.opExtrude","CAP_EDGE",EDGE,{"disambiguationData":[OSD([sQuery(id+"F6.wireOp",EDGE,"E10.23.3")])],"isStart":true});
            var Q110;
            Q110=makeQuery(id+"F7.opExtrude","CAP_EDGE",EDGE,{"disambiguationData":[OSD([sQuery(id+"F6.wireOp",EDGE,"E10.43.3")])],"isStart":true});
            var Q111;
            Q111=makeQuery(id+"F7.opExtrude","CAP_EDGE",EDGE,{"disambiguationData":[OSD([sQuery(id+"F6.wireOp",EDGE,"E5")])],"isStart":true});
            var Q112;
            Q112=makeQuery(id+"F7.opExtrude","CAP_EDGE",EDGE,{"disambiguationData":[OSD([sQuery(id+"F6.wireOp",EDGE,"E10.26.0")])],"isStart":true});
            var Q113;
            Q113=makeQuery(id+"F7.opExtrude","CAP_EDGE",EDGE,{"disambiguationData":[OSD([sQuery(id+"F6.wireOp",EDGE,"E10.42.0")])],"isStart":true});
            var Q114;
            Q114=makeQuery(id+"F7.opExtrude","CAP_EDGE",EDGE,{"disambiguationData":[OSD([sQuery(id+"F6.wireOp",EDGE,"E10.31.0")])],"isStart":true});
            var Q115;
            Q115=makeQuery(id+"F7.opExtrude","CAP_EDGE",EDGE,{"disambiguationData":[OSD([sQuery(id+"F6.wireOp",EDGE,"E10.44.0")])],"isStart":true});
            var Q116;
            Q116=makeQuery(id+"F7.opExtrude","CAP_EDGE",EDGE,{"disambiguationData":[OSD([sQuery(id+"F6.wireOp",EDGE,"E10.49.0")])],"isStart":true});
            var Q117;
            Q117=makeQuery(id+"F7.opExtrude","CAP_EDGE",EDGE,{"disambiguationData":[OSD([sQuery(id+"F6.wireOp",EDGE,"E10.30.0")])],"isStart":true});
            var Q118;
            Q118=makeQuery(id+"F7.opExtrude","CAP_EDGE",EDGE,{"disambiguationData":[OSD([sQuery(id+"F6.wireOp",EDGE,"E10.38.0")])],"isStart":true});
            var Q119;
            Q119=makeQuery(id+"F7.opExtrude","CAP_EDGE",EDGE,{"disambiguationData":[OSD([sQuery(id+"F6.wireOp",EDGE,"E10.43.0")])],"isStart":true});
            var Q120;
            Q120=makeQuery(id+"F7.opExtrude","CAP_EDGE",EDGE,{"disambiguationData":[OSD([sQuery(id+"F6.wireOp",EDGE,"E10.32.0")])],"isStart":true});
            var Q121;
            Q121=makeQuery(id+"F7.opExtrude","CAP_EDGE",EDGE,{"disambiguationData":[OSD([sQuery(id+"F6.wireOp",EDGE,"E10.37.0")])],"isStart":true});
            var Q122;
            Q122=makeQuery(id+"F7.opExtrude","CAP_EDGE",EDGE,{"disambiguationData":[OSD([sQuery(id+"F6.wireOp",EDGE,"E10.45.0")])],"isStart":true});
            var Q123;
            Q123=makeQuery(id+"F7.opExtrude","CAP_EDGE",EDGE,{"disambiguationData":[OSD([sQuery(id+"F6.wireOp",EDGE,"E10.27.5")])],"isStart":true});
            var Q124;
            Q124=makeQuery(id+"F7.opExtrude","CAP_EDGE",EDGE,{"disambiguationData":[OSD([sQuery(id+"F6.wireOp",EDGE,"E10.35.5")])],"isStart":true});
            var Q125;
            Q125=makeQuery(id+"F7.opExtrude","CAP_EDGE",EDGE,{"disambiguationData":[OSD([sQuery(id+"F6.wireOp",EDGE,"E10.39.5")])],"isStart":true});
            var Q126;
            Q126=makeQuery(id+"F7.opExtrude","CAP_EDGE",EDGE,{"disambiguationData":[OSD([sQuery(id+"F6.wireOp",EDGE,"E10.43.5")])],"isStart":true});
            var Q127;
            {var subQ1=sQuery(id+"F6.wireOp",EDGE,"E3");var subQ2=sQuery(id+"F0.wireOp",EDGE,"E0");Q127=makeQuery(id+"F7.boolean.opBoolean","SPLIT",EDGE,{"disambiguationData":[TD([makeQuery(id+"F7.opExtrude","SWEPT_FACE",FACE,{"disambiguationData":[OSD([subQ1])]})])],"derivedFrom":makeQuery(id+"F1.opExtrude","CAP_EDGE",EDGE,{"disambiguationData":[OSD([subQ2])],"isStart":false})});}
            var Q128;
            {var subQ0=sQuery(id+"F6.wireOp",EDGE,"E10.31.5");var subQ2=sQuery(id+"F0.wireOp",EDGE,"E0");Q128=makeQuery(id+"F7.boolean.opBoolean","SPLIT",EDGE,{"disambiguationData":[TD([makeQuery(id+"F7.opExtrude","SWEPT_FACE",FACE,{"disambiguationData":[OSD([subQ0])]})])],"derivedFrom":makeQuery(id+"F1.opExtrude","CAP_EDGE",EDGE,{"disambiguationData":[OSD([subQ2])],"isStart":false})});}
            var Q129;
            {var subQ0=sQuery(id+"F6.wireOp",EDGE,"E10.32.5");var subQ2=sQuery(id+"F0.wireOp",EDGE,"E0");Q129=makeQuery(id+"F7.boolean.opBoolean","SPLIT",EDGE,{"disambiguationData":[TD([makeQuery(id+"F7.opExtrude","SWEPT_FACE",FACE,{"disambiguationData":[OSD([subQ0])]})])],"derivedFrom":makeQuery(id+"F1.opExtrude","CAP_EDGE",EDGE,{"disambiguationData":[OSD([subQ2])],"isStart":false})});}
            var Q130;
            Q130=makeQuery(id+"F7.opExtrude","CAP_EDGE",EDGE,{"disambiguationData":[OSD([sQuery(id+"F6.wireOp",EDGE,"E10.28.3")])],"isStart":true});
            var Q131;
            Q131=makeQuery(id+"F7.opExtrude","CAP_EDGE",EDGE,{"disambiguationData":[OSD([sQuery(id+"F6.wireOp",EDGE,"E10.36.3")])],"isStart":true});
            var Q132;
            Q132=makeQuery(id+"F7.opExtrude","CAP_EDGE",EDGE,{"disambiguationData":[OSD([sQuery(id+"F6.wireOp",EDGE,"E10.40.3")])],"isStart":true});
            var Q133;
            {var subQ0=sQuery(id+"F6.wireOp",EDGE,"E10.1.5");var subQ2=sQuery(id+"F0.wireOp",EDGE,"E0");Q133=makeQuery(id+"F7.boolean.opBoolean","SPLIT",EDGE,{"disambiguationData":[TD([makeQuery(id+"F7.opExtrude","SWEPT_FACE",FACE,{"disambiguationData":[OSD([subQ0])]})])],"derivedFrom":makeQuery(id+"F1.opExtrude","CAP_EDGE",EDGE,{"disambiguationData":[OSD([subQ2])],"isStart":false})});}
            var Q134;
            {var subQ0=sQuery(id+"F6.wireOp",EDGE,"E10.2.5");var subQ1=sQuery(id+"F0.wireOp",EDGE,"E0");Q134=makeQuery(id+"F7.boolean.opBoolean","SPLIT",EDGE,{"disambiguationData":[TD([makeQuery(id+"F7.opExtrude","SWEPT_FACE",FACE,{"disambiguationData":[OSD([subQ0])]})])],"derivedFrom":makeQuery(id+"F1.opExtrude","CAP_EDGE",EDGE,{"disambiguationData":[OSD([subQ1])],"isStart":false})});}
            var Q135;
            Q135=makeQuery(id+"F7.opExtrude","CAP_EDGE",EDGE,{"disambiguationData":[OSD([sQuery(id+"F6.wireOp",EDGE,"E10.28.5")])],"isStart":true});
            var Q136;
            Q136=makeQuery(id+"F7.opExtrude","CAP_EDGE",EDGE,{"disambiguationData":[OSD([sQuery(id+"F6.wireOp",EDGE,"E10.36.5")])],"isStart":true});
            var Q137;
            Q137=makeQuery(id+"F7.opExtrude","CAP_EDGE",EDGE,{"disambiguationData":[OSD([sQuery(id+"F6.wireOp",EDGE,"E10.40.5")])],"isStart":true});
            var Q138;
            Q138=makeQuery(id+"F7.opExtrude","CAP_EDGE",EDGE,{"disambiguationData":[OSD([sQuery(id+"F6.wireOp",EDGE,"E10.44.5")])],"isStart":true});
            var Q139;
            {var subQ0=sQuery(id+"F6.wireOp",EDGE,"E10.3.5");var subQ2=sQuery(id+"F0.wireOp",EDGE,"E0");Q139=makeQuery(id+"F7.boolean.opBoolean","SPLIT",EDGE,{"disambiguationData":[TD([makeQuery(id+"F7.opExtrude","SWEPT_FACE",FACE,{"disambiguationData":[OSD([subQ0])]})])],"derivedFrom":makeQuery(id+"F1.opExtrude","CAP_EDGE",EDGE,{"disambiguationData":[OSD([subQ2])],"isStart":false})});}
            var Q140;
            {var subQ0=sQuery(id+"F6.wireOp",EDGE,"E10.19.5");var subQ2=sQuery(id+"F0.wireOp",EDGE,"E0");Q140=makeQuery(id+"F7.boolean.opBoolean","SPLIT",EDGE,{"disambiguationData":[TD([makeQuery(id+"F7.opExtrude","SWEPT_FACE",FACE,{"disambiguationData":[OSD([subQ0])]})])],"derivedFrom":makeQuery(id+"F1.opExtrude","CAP_EDGE",EDGE,{"disambiguationData":[OSD([subQ2])],"isStart":false})});}
            var Q141;
            {var subQ0=sQuery(id+"F6.wireOp",EDGE,"E10.4.5");var subQ2=sQuery(id+"F0.wireOp",EDGE,"E0");Q141=makeQuery(id+"F7.boolean.opBoolean","SPLIT",EDGE,{"disambiguationData":[TD([makeQuery(id+"F7.opExtrude","SWEPT_FACE",FACE,{"disambiguationData":[OSD([subQ0])]})])],"derivedFrom":makeQuery(id+"F1.opExtrude","CAP_EDGE",EDGE,{"disambiguationData":[OSD([subQ2])],"isStart":false})});}
            var Q142;
            {var subQ0=sQuery(id+"F6.wireOp",EDGE,"E10.20.5");var subQ2=sQuery(id+"F0.wireOp",EDGE,"E0");Q142=makeQuery(id+"F7.boolean.opBoolean","SPLIT",EDGE,{"disambiguationData":[TD([makeQuery(id+"F7.opExtrude","SWEPT_FACE",FACE,{"disambiguationData":[OSD([subQ0])]})])],"derivedFrom":makeQuery(id+"F1.opExtrude","CAP_EDGE",EDGE,{"disambiguationData":[OSD([subQ2])],"isStart":false})});}
            var Q143;
            {var subQ0=sQuery(id+"F6.wireOp",EDGE,"E10.36.5");var subQ2=sQuery(id+"F0.wireOp",EDGE,"E0");Q143=makeQuery(id+"F7.boolean.opBoolean","SPLIT",EDGE,{"disambiguationData":[TD([makeQuery(id+"F7.opExtrude","SWEPT_FACE",FACE,{"disambiguationData":[OSD([subQ0])]})])],"derivedFrom":makeQuery(id+"F1.opExtrude","CAP_EDGE",EDGE,{"disambiguationData":[OSD([subQ2])],"isStart":false})});}
            var Q144;
            Q144=makeQuery(id+"F7.opExtrude","CAP_EDGE",EDGE,{"disambiguationData":[OSD([sQuery(id+"F6.wireOp",EDGE,"E10.25.3")])],"isStart":true});
            var Q145;
            Q145=makeQuery(id+"F7.opExtrude","CAP_EDGE",EDGE,{"disambiguationData":[OSD([sQuery(id+"F6.wireOp",EDGE,"E10.29.3")])],"isStart":true});
            var Q146;
            Q146=makeQuery(id+"F7.opExtrude","CAP_EDGE",EDGE,{"disambiguationData":[OSD([sQuery(id+"F6.wireOp",EDGE,"E10.37.3")])],"isStart":true});
            var Q147;
            {var subQ0=sQuery(id+"F6.wireOp",EDGE,"E10.37.5");var subQ2=sQuery(id+"F0.wireOp",EDGE,"E0");Q147=makeQuery(id+"F7.boolean.opBoolean","SPLIT",EDGE,{"disambiguationData":[TD([makeQuery(id+"F7.opExtrude","SWEPT_FACE",FACE,{"disambiguationData":[OSD([subQ0])]})])],"derivedFrom":makeQuery(id+"F1.opExtrude","CAP_EDGE",EDGE,{"disambiguationData":[OSD([subQ2])],"isStart":false})});}
            var Q148;
            {var subQ0=sQuery(id+"F6.wireOp",EDGE,"E10.38.5");var subQ2=sQuery(id+"F0.wireOp",EDGE,"E0");Q148=makeQuery(id+"F7.boolean.opBoolean","SPLIT",EDGE,{"disambiguationData":[TD([makeQuery(id+"F7.opExtrude","SWEPT_FACE",FACE,{"disambiguationData":[OSD([subQ0])]})])],"derivedFrom":makeQuery(id+"F1.opExtrude","CAP_EDGE",EDGE,{"disambiguationData":[OSD([subQ2])],"isStart":false})});}
            var Q149;
            Q149=makeQuery(id+"F7.opExtrude","CAP_EDGE",EDGE,{"disambiguationData":[OSD([sQuery(id+"F6.wireOp",EDGE,"E10.37.5")])],"isStart":true});
            var Q150;
            {var subQ0=sQuery(id+"F6.wireOp",EDGE,"E10.23.5");var subQ2=sQuery(id+"F0.wireOp",EDGE,"E0");Q150=makeQuery(id+"F7.boolean.opBoolean","SPLIT",EDGE,{"disambiguationData":[TD([makeQuery(id+"F7.opExtrude","SWEPT_FACE",FACE,{"disambiguationData":[OSD([subQ0])]})])],"derivedFrom":makeQuery(id+"F1.opExtrude","CAP_EDGE",EDGE,{"disambiguationData":[OSD([subQ2])],"isStart":false})});}
            var Q151;
            {var subQ0=sQuery(id+"F6.wireOp",EDGE,"E10.24.5");var subQ1=sQuery(id+"F0.wireOp",EDGE,"E0");Q151=makeQuery(id+"F7.boolean.opBoolean","SPLIT",EDGE,{"disambiguationData":[TD([makeQuery(id+"F7.opExtrude","SWEPT_FACE",FACE,{"disambiguationData":[OSD([subQ0])]})])],"derivedFrom":makeQuery(id+"F1.opExtrude","CAP_EDGE",EDGE,{"disambiguationData":[OSD([subQ1])],"isStart":false})});}
            var Q152;
            {var subQ0=sQuery(id+"F6.wireOp",EDGE,"E10.40.5");var subQ2=sQuery(id+"F0.wireOp",EDGE,"E0");Q152=makeQuery(id+"F7.boolean.opBoolean","SPLIT",EDGE,{"disambiguationData":[TD([makeQuery(id+"F7.opExtrude","SWEPT_FACE",FACE,{"disambiguationData":[OSD([subQ0])]})])],"derivedFrom":makeQuery(id+"F1.opExtrude","CAP_EDGE",EDGE,{"disambiguationData":[OSD([subQ2])],"isStart":false})});}
            var Q153;
            Q153=makeQuery(id+"F7.opExtrude","CAP_EDGE",EDGE,{"disambiguationData":[OSD([sQuery(id+"F6.wireOp",EDGE,"E10.34.3")])],"isStart":true});
            var Q154;
            Q154=makeQuery(id+"F7.opExtrude","CAP_EDGE",EDGE,{"disambiguationData":[OSD([sQuery(id+"F6.wireOp",EDGE,"E10.38.3")])],"isStart":true});
            var Q155;
            Q155=makeQuery(id+"F7.opExtrude","CAP_EDGE",EDGE,{"disambiguationData":[OSD([sQuery(id+"F6.wireOp",EDGE,"E10.42.3")])],"isStart":true});
            var Q156;
            {var subQ0=sQuery(id+"F6.wireOp",EDGE,"E10.41.5");var subQ2=sQuery(id+"F0.wireOp",EDGE,"E0");Q156=makeQuery(id+"F7.boolean.opBoolean","SPLIT",EDGE,{"disambiguationData":[TD([makeQuery(id+"F7.opExtrude","SWEPT_FACE",FACE,{"disambiguationData":[OSD([subQ0])]})])],"derivedFrom":makeQuery(id+"F1.opExtrude","CAP_EDGE",EDGE,{"disambiguationData":[OSD([subQ2])],"isStart":false})});}
            var Q157;
            {var subQ0=sQuery(id+"F6.wireOp",EDGE,"E10.42.5");var subQ2=sQuery(id+"F0.wireOp",EDGE,"E0");Q157=makeQuery(id+"F7.boolean.opBoolean","SPLIT",EDGE,{"disambiguationData":[TD([makeQuery(id+"F7.opExtrude","SWEPT_FACE",FACE,{"disambiguationData":[OSD([subQ0])]})])],"derivedFrom":makeQuery(id+"F1.opExtrude","CAP_EDGE",EDGE,{"disambiguationData":[OSD([subQ2])],"isStart":false})});}
            var Q158;
            Q158=makeQuery(id+"F7.opExtrude","CAP_EDGE",EDGE,{"disambiguationData":[OSD([sQuery(id+"F6.wireOp",EDGE,"E10.30.5")])],"isStart":true});
            var Q159;
            Q159=makeQuery(id+"F7.opExtrude","CAP_EDGE",EDGE,{"disambiguationData":[OSD([sQuery(id+"F6.wireOp",EDGE,"E10.34.5")])],"isStart":true});
            var Q160;
            Q160=makeQuery(id+"F7.opExtrude","CAP_EDGE",EDGE,{"disambiguationData":[OSD([sQuery(id+"F6.wireOp",EDGE,"E10.38.5")])],"isStart":true});
            var Q161;
            {var subQ0=sQuery(id+"F6.wireOp",EDGE,"E10.43.5");var subQ2=sQuery(id+"F0.wireOp",EDGE,"E0");Q161=makeQuery(id+"F7.boolean.opBoolean","SPLIT",EDGE,{"disambiguationData":[TD([makeQuery(id+"F7.opExtrude","SWEPT_FACE",FACE,{"disambiguationData":[OSD([subQ0])]})])],"derivedFrom":makeQuery(id+"F1.opExtrude","CAP_EDGE",EDGE,{"disambiguationData":[OSD([subQ2])],"isStart":false})});}
            var Q162;
            {var subQ0=sQuery(id+"F6.wireOp",EDGE,"E10.28.5");var subQ1=sQuery(id+"F0.wireOp",EDGE,"E0");Q162=makeQuery(id+"F7.boolean.opBoolean","SPLIT",EDGE,{"disambiguationData":[TD([makeQuery(id+"F7.opExtrude","SWEPT_FACE",FACE,{"disambiguationData":[OSD([subQ0])]})])],"derivedFrom":makeQuery(id+"F1.opExtrude","CAP_EDGE",EDGE,{"disambiguationData":[OSD([subQ1])],"isStart":false})});}
            var Q163;
            {var subQ0=sQuery(id+"F6.wireOp",EDGE,"E10.44.5");var subQ2=sQuery(id+"F0.wireOp",EDGE,"E0");Q163=makeQuery(id+"F7.boolean.opBoolean","SPLIT",EDGE,{"disambiguationData":[TD([makeQuery(id+"F7.opExtrude","SWEPT_FACE",FACE,{"disambiguationData":[OSD([subQ0])]})])],"derivedFrom":makeQuery(id+"F1.opExtrude","CAP_EDGE",EDGE,{"disambiguationData":[OSD([subQ2])],"isStart":false})});}
            var Q164;
            Q164=makeQuery(id+"F7.opExtrude","CAP_EDGE",EDGE,{"disambiguationData":[OSD([sQuery(id+"F6.wireOp",EDGE,"E10.35.3")])],"isStart":true});
            var Q165;
            Q165=makeQuery(id+"F7.opExtrude","CAP_EDGE",EDGE,{"disambiguationData":[OSD([sQuery(id+"F6.wireOp",EDGE,"E10.39.3")])],"isStart":true});
            var Q166;
            Q166=makeQuery(id+"F7.opExtrude","CAP_EDGE",EDGE,{"disambiguationData":[OSD([sQuery(id+"F6.wireOp",EDGE,"E10.47.3")])],"isStart":true});
            var Q167;
            Q167=makeQuery(id+"F7.opExtrude","CAP_EDGE",EDGE,{"disambiguationData":[OSD([sQuery(id+"F6.wireOp",EDGE,"E10.28.0")])],"isStart":true});
            var Q168;
            Q168=makeQuery(id+"F7.opExtrude","CAP_EDGE",EDGE,{"disambiguationData":[OSD([sQuery(id+"F6.wireOp",EDGE,"E10.46.0")])],"isStart":true});
            var Q169;
            Q169=makeQuery(id+"F7.opExtrude","CAP_EDGE",EDGE,{"disambiguationData":[OSD([sQuery(id+"F6.wireOp",EDGE,"E10.29.0")])],"isStart":true});
            var Q170;
            {var subQ0=sQuery(id+"F6.wireOp",EDGE,"E10.30.5");var subQ2=sQuery(id+"F0.wireOp",EDGE,"E0");Q170=makeQuery(id+"F7.boolean.opBoolean","SPLIT",EDGE,{"disambiguationData":[TD([makeQuery(id+"F7.opExtrude","SWEPT_FACE",FACE,{"disambiguationData":[OSD([subQ0])]})])],"derivedFrom":makeQuery(id+"F1.opExtrude","CAP_EDGE",EDGE,{"disambiguationData":[OSD([subQ2])],"isStart":false})});}
            var Q171;
            {var subQ0=sQuery(id+"F6.wireOp",EDGE,"E10.46.5");var subQ1=sQuery(id+"F0.wireOp",EDGE,"E0");Q171=makeQuery(id+"F7.boolean.opBoolean","SPLIT",EDGE,{"disambiguationData":[TD([makeQuery(id+"F7.opExtrude","SWEPT_FACE",FACE,{"disambiguationData":[OSD([subQ0])]})])],"derivedFrom":makeQuery(id+"F1.opExtrude","CAP_EDGE",EDGE,{"disambiguationData":[OSD([subQ1])],"isStart":false})});}
            var Q172;
            Q172=makeQuery(id+"F7.opExtrude","CAP_EDGE",EDGE,{"disambiguationData":[OSD([sQuery(id+"F6.wireOp",EDGE,"E10.47.5")])],"isStart":true});
            var Q173;
            {var subQ0=sQuery(id+"F6.wireOp",EDGE,"E10.47.5");var subQ2=sQuery(id+"F0.wireOp",EDGE,"E0");Q173=makeQuery(id+"F7.boolean.opBoolean","SPLIT",EDGE,{"disambiguationData":[TD([makeQuery(id+"F7.opExtrude","SWEPT_FACE",FACE,{"disambiguationData":[OSD([subQ0])]})])],"derivedFrom":makeQuery(id+"F1.opExtrude","CAP_EDGE",EDGE,{"disambiguationData":[OSD([subQ2])],"isStart":false})});}
            var Q174;
            {var subQ0=sQuery(id+"F6.wireOp",EDGE,"E5");var subQ1=sQuery(id+"F0.wireOp",EDGE,"E0");Q174=makeQuery(id+"F7.boolean.opBoolean","SPLIT",EDGE,{"disambiguationData":[TD([makeQuery(id+"F7.opExtrude","SWEPT_FACE",FACE,{"disambiguationData":[OSD([subQ0])]})])],"derivedFrom":makeQuery(id+"F1.opExtrude","CAP_EDGE",EDGE,{"disambiguationData":[OSD([subQ1])],"isStart":false})});}
            var Q175;
            {var subQ0=sQuery(id+"F6.wireOp",EDGE,"E10.48.5");var subQ2=sQuery(id+"F0.wireOp",EDGE,"E0");Q175=makeQuery(id+"F7.boolean.opBoolean","SPLIT",EDGE,{"disambiguationData":[TD([makeQuery(id+"F7.opExtrude","SWEPT_FACE",FACE,{"disambiguationData":[OSD([subQ0])]})])],"derivedFrom":makeQuery(id+"F1.opExtrude","CAP_EDGE",EDGE,{"disambiguationData":[OSD([subQ2])],"isStart":false})});}
            var Q176;
            Q176=makeQuery(id+"F7.opExtrude","CAP_EDGE",EDGE,{"disambiguationData":[OSD([sQuery(id+"F6.wireOp",EDGE,"E10.32.3")])],"isStart":true});
            var Q177;
            Q177=makeQuery(id+"F7.opExtrude","CAP_EDGE",EDGE,{"disambiguationData":[OSD([sQuery(id+"F6.wireOp",EDGE,"E10.48.3")])],"isStart":true});
            var Q178;
            Q178=makeQuery(id+"F7.opExtrude","CAP_EDGE",EDGE,{"disambiguationData":[OSD([sQuery(id+"F6.wireOp",EDGE,"E10.33.3")])],"isStart":true});
            var Q179;
            Q179=makeQuery(id+"F7.opExtrude","CAP_EDGE",EDGE,{"disambiguationData":[OSD([sQuery(id+"F6.wireOp",EDGE,"E10.49.3")])],"isStart":true});
            var Q180;
            Q180=makeQuery(id+"F7.opExtrude","CAP_EDGE",EDGE,{"disambiguationData":[OSD([sQuery(id+"F6.wireOp",EDGE,"E10.25.5")])],"isStart":true});
            var Q181;
            Q181=makeQuery(id+"F7.opExtrude","CAP_EDGE",EDGE,{"disambiguationData":[OSD([sQuery(id+"F6.wireOp",EDGE,"E10.41.5")])],"isStart":true});
            var Q182;
            Q182=makeQuery(id+"F7.opExtrude","CAP_EDGE",EDGE,{"disambiguationData":[OSD([sQuery(id+"F6.wireOp",EDGE,"E10.45.5")])],"isStart":true});
            var Q183;
            Q183=makeQuery(id+"F7.opExtrude","CAP_EDGE",EDGE,{"disambiguationData":[OSD([sQuery(id+"F6.wireOp",EDGE,"E10.49.5")])],"isStart":true});
            var Q184;
            Q184=makeQuery(id+"F7.opExtrude","CAP_EDGE",EDGE,{"disambiguationData":[OSD([sQuery(id+"F6.wireOp",EDGE,"E10.30.3")])],"isStart":true});
            var Q185;
            {var subQ0=sQuery(id+"F6.wireOp",EDGE,"E10.26.5");var subQ2=sQuery(id+"F0.wireOp",EDGE,"E0");Q185=makeQuery(id+"F7.boolean.opBoolean","SPLIT",EDGE,{"disambiguationData":[TD([makeQuery(id+"F7.opExtrude","SWEPT_FACE",FACE,{"disambiguationData":[OSD([subQ0])]})])],"derivedFrom":makeQuery(id+"F1.opExtrude","CAP_EDGE",EDGE,{"disambiguationData":[OSD([subQ2])],"isStart":false})});}
            var Q186;
            Q186=makeQuery(id+"F7.opExtrude","CAP_EDGE",EDGE,{"disambiguationData":[OSD([sQuery(id+"F6.wireOp",EDGE,"E10.42.5")])],"isStart":true});
            var Q187;
            Q187=makeQuery(id+"F7.opExtrude","CAP_EDGE",EDGE,{"disambiguationData":[OSD([sQuery(id+"F6.wireOp",EDGE,"E10.46.5")])],"isStart":true});
            var Q188;
            {var subQ0=sQuery(id+"F6.wireOp",EDGE,"E10.27.5");var subQ2=sQuery(id+"F0.wireOp",EDGE,"E0");Q188=makeQuery(id+"F7.boolean.opBoolean","SPLIT",EDGE,{"disambiguationData":[TD([makeQuery(id+"F7.opExtrude","SWEPT_FACE",FACE,{"disambiguationData":[OSD([subQ0])]})])],"derivedFrom":makeQuery(id+"F1.opExtrude","CAP_EDGE",EDGE,{"disambiguationData":[OSD([subQ2])],"isStart":false})});}
            var Q189;
            {var subQ0=sQuery(id+"F6.wireOp",EDGE,"E10.29.5");var subQ2=sQuery(id+"F0.wireOp",EDGE,"E0");Q189=makeQuery(id+"F7.boolean.opBoolean","SPLIT",EDGE,{"disambiguationData":[TD([makeQuery(id+"F7.opExtrude","SWEPT_FACE",FACE,{"disambiguationData":[OSD([subQ0])]})])],"derivedFrom":makeQuery(id+"F1.opExtrude","CAP_EDGE",EDGE,{"disambiguationData":[OSD([subQ2])],"isStart":false})});}
            var Q190;
            {var subQ0=sQuery(id+"F6.wireOp",EDGE,"E10.45.5");var subQ2=sQuery(id+"F0.wireOp",EDGE,"E0");Q190=makeQuery(id+"F7.boolean.opBoolean","SPLIT",EDGE,{"disambiguationData":[TD([makeQuery(id+"F7.opExtrude","SWEPT_FACE",FACE,{"disambiguationData":[OSD([subQ0])]})])],"derivedFrom":makeQuery(id+"F1.opExtrude","CAP_EDGE",EDGE,{"disambiguationData":[OSD([subQ2])],"isStart":false})});}
            var Q191;
            Q191=makeQuery(id+"F7.opExtrude","CAP_EDGE",EDGE,{"disambiguationData":[OSD([sQuery(id+"F6.wireOp",EDGE,"E10.47.0")])],"isStart":true});
            var Q192;
            Q192=makeQuery(id+"F7.opExtrude","CAP_EDGE",EDGE,{"disambiguationData":[OSD([sQuery(id+"F6.wireOp",EDGE,"E10.48.0")])],"isStart":true});
            var Q193;
            Q193=makeQuery(id+"F7.opExtrude","CAP_EDGE",EDGE,{"disambiguationData":[OSD([sQuery(id+"F6.wireOp",EDGE,"E10.48.5")])],"isStart":true});
            var Q194;
            Q194=makeQuery(id+"F7.opExtrude","CAP_EDGE",EDGE,{"disambiguationData":[OSD([sQuery(id+"F6.wireOp",EDGE,"E10.26.3")])],"isStart":true});
            var Q195;
            {var subQ0=sQuery(id+"F6.wireOp",EDGE,"E10.25.5");var subQ2=sQuery(id+"F0.wireOp",EDGE,"E0");Q195=makeQuery(id+"F7.boolean.opBoolean","SPLIT",EDGE,{"disambiguationData":[TD([makeQuery(id+"F7.opExtrude","SWEPT_FACE",FACE,{"disambiguationData":[OSD([subQ0])]})])],"derivedFrom":makeQuery(id+"F1.opExtrude","CAP_EDGE",EDGE,{"disambiguationData":[OSD([subQ2])],"isStart":false})});}
            var Q196;
            Q196=makeQuery(id+"F7.opExtrude","CAP_EDGE",EDGE,{"disambiguationData":[OSD([sQuery(id+"F6.wireOp",EDGE,"E10.26.5")])],"isStart":true});
            var Q197;
            Q197=makeQuery(id+"F7.opExtrude","CAP_EDGE",EDGE,{"disambiguationData":[OSD([sQuery(id+"F6.wireOp",EDGE,"E10.27.3")])],"isStart":true});
            var Q198;
            Q198=makeQuery(id+"F7.opExtrude","CAP_EDGE",EDGE,{"disambiguationData":[OSD([sQuery(id+"F6.wireOp",EDGE,"E10.31.3")])],"isStart":true});
            var Q199;
            Q199=makeQuery(id+"F7.opExtrude","CAP_EDGE",EDGE,{"disambiguationData":[OSD([sQuery(id+"F6.wireOp",EDGE,"E10.27.0")])],"isStart":true});
            fillet(context, id + "F8", {"entities" : qUnion([Q0, Q1, Q2, Q3, Q4, Q5, Q6, Q7, Q8, Q9, Q10, Q11, Q12, Q13, Q14, Q15, Q16, Q17, Q18, Q19, Q20, Q21, Q22, Q23, Q24, Q25, Q26, Q27, Q28, Q29, Q30, Q31, Q32, Q33, Q34, Q35, Q36, Q37, Q38, Q39, Q40, Q41, Q42, Q43, Q44, Q45, Q46, Q47, Q48, Q49, Q50, Q51, Q52, Q53, Q54, Q55, Q56, Q57, Q58, Q59, Q60, Q61, Q62, Q63, Q64, Q65, Q66, Q67, Q68, Q69, Q70, Q71, Q72, Q73, Q74, Q75, Q76, Q77, Q78, Q79, Q80, Q81, Q82, Q83, Q84, Q85, Q86, Q87, Q88, Q89, Q90, Q91, Q92, Q93, Q94, Q95, Q96, Q97, Q98, Q99, Q100, Q101, Q102, Q103, Q104, Q105, Q106, Q107, Q108, Q109, Q110, Q111, Q112, Q113, Q114, Q115, Q116, Q117, Q118, Q119, Q120, Q121, Q122, Q123, Q124, Q125, Q126, Q127, Q128, Q129, Q130, Q131, Q132, Q133, Q134, Q135, Q136, Q137, Q138, Q139, Q140, Q141, Q142, Q143, Q144, Q145, Q146, Q147, Q148, Q149, Q150, Q151, Q152, Q153, Q154, Q155, Q156, Q157, Q158, Q159, Q160, Q161, Q162, Q163, Q164, Q165, Q166, Q167, Q168, Q169, Q170, Q171, Q172, Q173, Q174, Q175, Q176, Q177, Q178, Q179, Q180, Q181, Q182, Q183, Q184, Q185, Q186, Q187, Q188, Q189, Q190, Q191, Q192, Q193, Q194, Q195, Q196, Q197, Q198, Q199]), "radius" : 2 * mm, "tangentPropagation" : true, "allowEdgeOverflow" : false});
        }
    });
